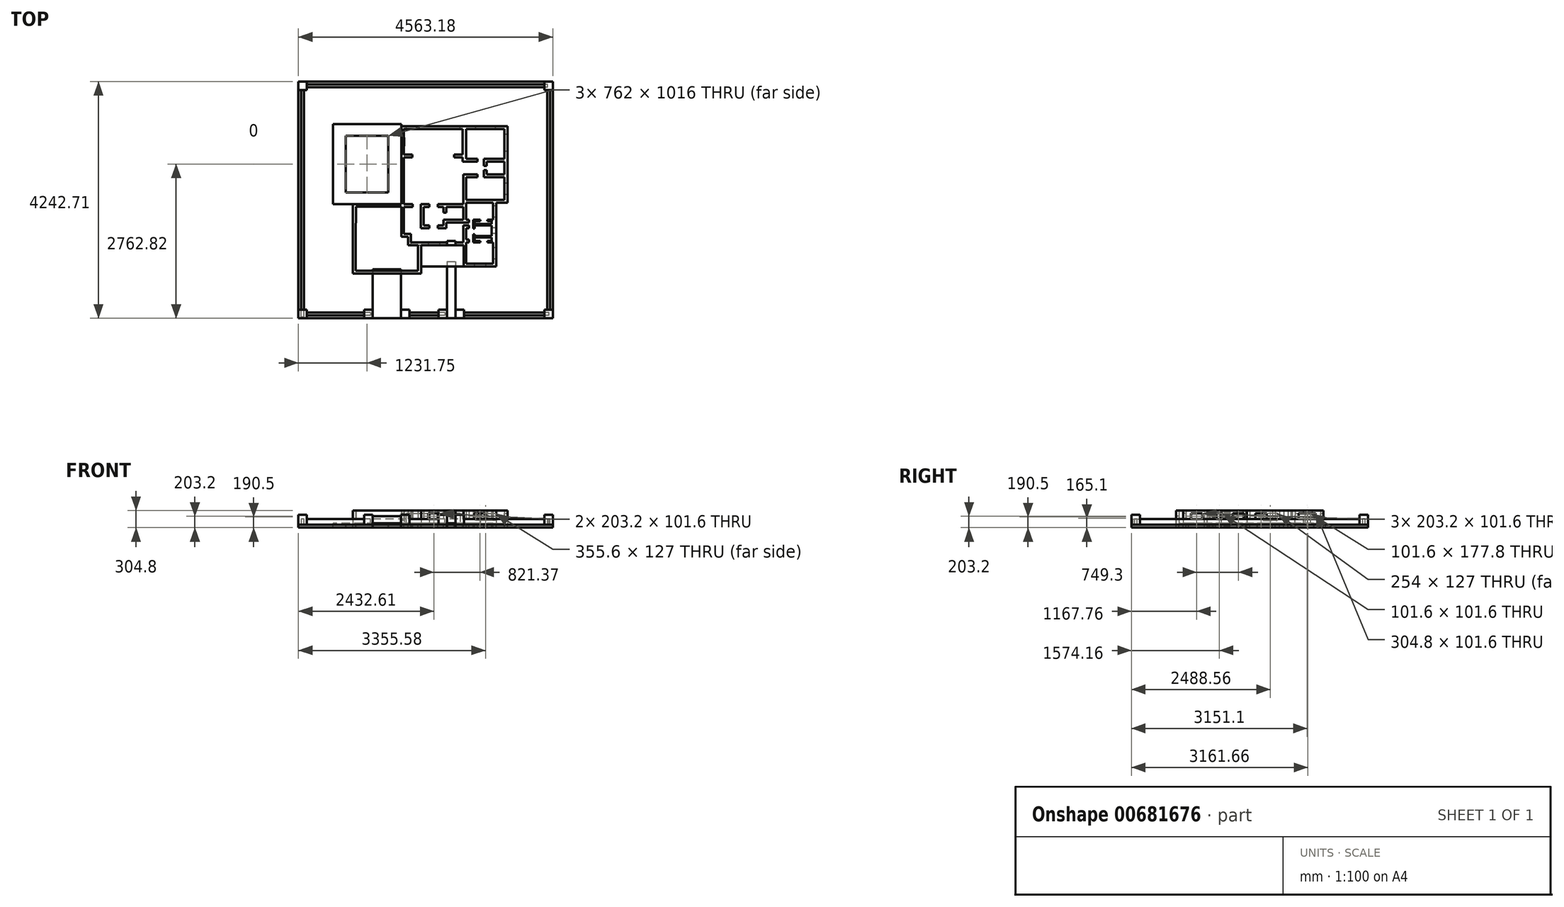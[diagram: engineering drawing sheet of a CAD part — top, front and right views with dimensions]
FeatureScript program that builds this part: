
annotation { "Feature Type Name" : "Feature", "Feature Type Description" : "" }
export const myFeature = defineFeature(function(context is Context, id is Id, definition is map)
    precondition{}
    {
        {
            var Q0;
            Q0=qCreatedBy(makeId("Top.planeOp"),FACE);
            var sketch = newSketch(context, id + "F0", { "sketchPlane" : qUnion([Q0])});
            skLineSegment(sketch, "E0", {"start": v(0, 0) * mm, "end": v(533.4, 0) * mm});
            skLineSegment(sketch, "E1", {"start": v(1396.8, 508) * mm, "end": v(1396.8, 127) * mm});
            skLineSegment(sketch, "E2", {"start": v(1396.8, 127) * mm, "end": v(1879.4, 127) * mm});
            skLineSegment(sketch, "E3", {"start": v(1828.6, 1270) * mm, "end": v(2082.6, 1270) * mm});
            skLineSegment(sketch, "E4", {"start": v(2082.6, 2540) * mm, "end": v(1396.8, 2540) * mm});
            skLineSegment(sketch, "E5", {"start": v(231.53, 1150.6) * mm, "end": v(-301.87, 1150.6) * mm});
            skLineSegment(sketch, "E6", {"start": v(-304.8, 1192.71) * mm, "end": v(177.8, 1192.71) * mm});
            skLineSegment(sketch, "E7", {"start": v(-47.87, -51.89) * mm, "end": v(587.13, -51.89) * mm});
            skLineSegment(sketch, "E8", {"start": v(587.13, -51.89) * mm, "end": v(587.13, 456.11) * mm});
            skLineSegment(sketch, "E9", {"start": v(587.13, 456.11) * mm, "end": v(1349.13, 456.11) * mm});
            skLineSegment(sketch, "E10", {"start": v(1349.13, 456.11) * mm, "end": v(1349.13, 75.11) * mm});
            skLineSegment(sketch, "E11", {"start": v(1349.13, 75.11) * mm, "end": v(1933.33, 75.11) * mm});
            skLineSegment(sketch, "E12", {"start": v(2136.53, 1218.11) * mm, "end": v(2136.53, 2589.71) * mm});
            skLineSegment(sketch, "E13", {"start": v(2136.53, 2589.71) * mm, "end": v(1349.13, 2589.71) * mm});
            skLineSegment(sketch, "E14", {"start": v(533.4, 456.11) * mm, "end": v(482.6, 456.11) * mm});
            skLineSegment(sketch, "E15", {"start": v(482.6, 456.11) * mm, "end": v(355.6, 456.11) * mm});
            skLineSegment(sketch, "E16", {"start": v(355.6, 456.11) * mm, "end": v(355.6, 608.51) * mm});
            skLineSegment(sketch, "E17", {"start": v(355.6, 608.51) * mm, "end": v(231.53, 608.51) * mm});
            skLineSegment(sketch, "E18", {"start": v(231.53, 608.51) * mm, "end": v(231.53, 1150.6) * mm});
            skLineSegment(sketch, "E19", {"start": v(279.4, 1143) * mm, "end": v(279.4, 660.4) * mm});
            skLineSegment(sketch, "E20", {"start": v(406.4, 508) * mm, "end": v(533.4, 508) * mm});
            skLineSegment(sketch, "E21", {"start": v(177.8, 1192.71) * mm, "end": v(231.53, 1192.71) * mm});
            skLineSegment(sketch, "E22", {"start": v(231.53, 1192.71) * mm, "end": v(231.53, 2081.71) * mm});
            skLineSegment(sketch, "E23", {"start": v(533.4, 456.11) * mm, "end": v(533.4, 0) * mm});
            skLineSegment(sketch, "E24", {"start": v(1828.6, 1219.2) * mm, "end": v(1396.8, 1219.2) * mm});
            skLineSegment(sketch, "E25", {"start": v(1933.33, 75.11) * mm, "end": v(1933.33, 1218.11) * mm});
            skLineSegment(sketch, "E26", {"start": v(1933.33, 1218.11) * mm, "end": v(2136.53, 1218.11) * mm});
            skLineSegment(sketch, "E27", {"start": v(1879.4, 127) * mm, "end": v(1879.4, 1219.2) * mm});
            skLineSegment(sketch, "E28", {"start": v(1879.4, 1219.2) * mm, "end": v(1828.6, 1219.2) * mm});
            skLineSegment(sketch, "E29", {"start": v(1396.8, 508) * mm, "end": v(1447.6, 508) * mm});
            skLineSegment(sketch, "E30", {"start": v(1523.8, 508) * mm, "end": v(1650.8, 508) * mm});
            skLineSegment(sketch, "E31", {"start": v(1879.4, 508) * mm, "end": v(1777.8, 508) * mm});
            skLineSegment(sketch, "E32", {"start": v(1523.8, 508) * mm, "end": v(1523.8, 596.9) * mm});
            skLineSegment(sketch, "E33", {"start": v(1879.4, 811.34) * mm, "end": v(1879.4, 749.31) * mm});
            skLineSegment(sketch, "E34", {"start": v(1523.8, 914.4) * mm, "end": v(1650.8, 914.4) * mm});
            skLineSegment(sketch, "E35", {"start": v(1879.4, 914.4) * mm, "end": v(1777.8, 914.4) * mm});
            skLineSegment(sketch, "E36", {"start": v(1523.8, 596.9) * mm, "end": v(1523.8, 650.75) * mm});
            skLineSegment(sketch, "E37", {"start": v(1523.8, 811.34) * mm, "end": v(1523.8, 757.49) * mm});
            skLineSegment(sketch, "E38", {"start": v(1396.8, 965.2) * mm, "end": v(1396.8, 1219.2) * mm});
            skLineSegment(sketch, "E39", {"start": v(1650.8, 914.4) * mm, "end": v(1650.8, 889) * mm});
            skLineSegment(sketch, "E40", {"start": v(1650.8, 889) * mm, "end": v(1549.2, 889) * mm});
            skLineSegment(sketch, "E41", {"start": v(1549.2, 889) * mm, "end": v(1549.2, 838.2) * mm});
            skLineSegment(sketch, "E42", {"start": v(1549.2, 838.2) * mm, "end": v(1854, 838.2) * mm});
            skLineSegment(sketch, "E43", {"start": v(1854, 838.2) * mm, "end": v(1854, 889) * mm});
            skLineSegment(sketch, "E44", {"start": v(1854, 889) * mm, "end": v(1777.8, 889) * mm});
            skLineSegment(sketch, "E45", {"start": v(1777.8, 889) * mm, "end": v(1777.8, 914.4) * mm});
            skLineSegment(sketch, "E46", {"start": v(1523.8, 757.49) * mm, "end": v(1549.2, 757.49) * mm});
            skLineSegment(sketch, "E47", {"start": v(1549.2, 757.49) * mm, "end": v(1549.2, 811.34) * mm});
            skLineSegment(sketch, "E48", {"start": v(1549.2, 811.34) * mm, "end": v(1854, 811.34) * mm});
            skLineSegment(sketch, "E49", {"start": v(1854, 811.34) * mm, "end": v(1854, 622.3) * mm});
            skLineSegment(sketch, "E50", {"start": v(1854, 622.3) * mm, "end": v(1549.2, 622.3) * mm});
            skLineSegment(sketch, "E51", {"start": v(1549.2, 622.3) * mm, "end": v(1549.2, 650.75) * mm});
            skLineSegment(sketch, "E52", {"start": v(1549.2, 650.75) * mm, "end": v(1523.8, 650.75) * mm});
            skLineSegment(sketch, "E53", {"start": v(1650.8, 508) * mm, "end": v(1650.8, 533.4) * mm});
            skLineSegment(sketch, "E54", {"start": v(1650.8, 533.4) * mm, "end": v(1549.2, 533.4) * mm});
            skLineSegment(sketch, "E55", {"start": v(1549.2, 533.4) * mm, "end": v(1549.2, 596.9) * mm});
            skLineSegment(sketch, "E56", {"start": v(1549.2, 596.9) * mm, "end": v(1854, 596.9) * mm});
            skLineSegment(sketch, "E57", {"start": v(1854, 596.9) * mm, "end": v(1854, 533.4) * mm});
            skLineSegment(sketch, "E58", {"start": v(1854, 533.4) * mm, "end": v(1777.8, 533.4) * mm});
            skLineSegment(sketch, "E59", {"start": v(1777.8, 533.4) * mm, "end": v(1777.8, 508) * mm});
            skLineSegment(sketch, "E60", {"start": v(1447.6, 508) * mm, "end": v(1447.6, 558.8) * mm});
            skLineSegment(sketch, "E61", {"start": v(1447.6, 558.8) * mm, "end": v(1396.8, 558.8) * mm});
            skLineSegment(sketch, "E62", {"start": v(1396.8, 558.8) * mm, "end": v(1396.8, 762) * mm});
            skLineSegment(sketch, "E63", {"start": v(1396.8, 965.2) * mm, "end": v(1396.8, 914.4) * mm});
            skLineSegment(sketch, "E64", {"start": v(1714.5, 1678.02) * mm, "end": v(2082.6, 1678.02) * mm});
            skLineSegment(sketch, "E65", {"start": v(1331.87, 2032) * mm, "end": v(1331.87, 1957.42) * mm});
            skLineSegment(sketch, "E66", {"start": v(1331.87, 1957.42) * mm, "end": v(1600.2, 1957.42) * mm});
            skLineSegment(sketch, "E67", {"start": v(1600.2, 1957.42) * mm, "end": v(1600.2, 2008.22) * mm});
            skLineSegment(sketch, "E68", {"start": v(1600.2, 2008.22) * mm, "end": v(1396.8, 2008.22) * mm});
            skLineSegment(sketch, "E69", {"start": v(1396.8, 2008.22) * mm, "end": v(1396.8, 2540) * mm});
            skLineSegment(sketch, "E70", {"start": v(1714.5, 1957.42) * mm, "end": v(1714.5, 2008.22) * mm});
            skLineSegment(sketch, "E71", {"start": v(1714.5, 2008.22) * mm, "end": v(2082.6, 2008.22) * mm});
            skLineSegment(sketch, "E72", {"start": v(2082.6, 2008.22) * mm, "end": v(2082.6, 2540) * mm});
            skLineSegment(sketch, "E73", {"start": v(1714.5, 1678.02) * mm, "end": v(1714.5, 1728.82) * mm});
            skLineSegment(sketch, "E74", {"start": v(2082.6, 1728.82) * mm, "end": v(2082.6, 1957.42) * mm});
            skLineSegment(sketch, "E75", {"start": v(2082.6, 1270) * mm, "end": v(2082.6, 1678.02) * mm});
            skLineSegment(sketch, "E76", {"start": v(1828.6, 1270) * mm, "end": v(1396.8, 1270) * mm});
            skLineSegment(sketch, "E77", {"start": v(1396.8, 1270) * mm, "end": v(1396.8, 1678.02) * mm});
            skLineSegment(sketch, "E78", {"start": v(1346, 1574.8) * mm, "end": v(1346, 1728.82) * mm});
            skLineSegment(sketch, "E79", {"start": v(1346, 1728.82) * mm, "end": v(1600.2, 1728.82) * mm});
            skLineSegment(sketch, "E80", {"start": v(1600.2, 1728.82) * mm, "end": v(1600.2, 1678.02) * mm});
            skLineSegment(sketch, "E81", {"start": v(1600.2, 1678.02) * mm, "end": v(1396.8, 1678.02) * mm});
            skLineSegment(sketch, "E82", {"start": v(1714.5, 1957.42) * mm, "end": v(1714.5, 1881.22) * mm});
            skLineSegment(sketch, "E83", {"start": v(1714.5, 1728.82) * mm, "end": v(1714.5, 1805.02) * mm});
            skLineSegment(sketch, "E84", {"start": v(1714.5, 1805.02) * mm, "end": v(1765.3, 1805.02) * mm});
            skLineSegment(sketch, "E85", {"start": v(1765.3, 1805.02) * mm, "end": v(1765.3, 1728.82) * mm});
            skLineSegment(sketch, "E86", {"start": v(1765.3, 1728.82) * mm, "end": v(2082.6, 1728.82) * mm});
            skLineSegment(sketch, "E87", {"start": v(1714.5, 1881.22) * mm, "end": v(1765.3, 1881.22) * mm});
            skLineSegment(sketch, "E88", {"start": v(1765.3, 1881.22) * mm, "end": v(1765.3, 1957.42) * mm});
            skLineSegment(sketch, "E89", {"start": v(1765.3, 1957.42) * mm, "end": v(2082.6, 1957.42) * mm});
            skLineSegment(sketch, "E90", {"start": v(-635, 508) * mm, "end": v(-635, 1192.71) * mm});
            skLineSegment(sketch, "E91", {"start": v(-635, 1192.71) * mm, "end": v(-304.8, 1192.71) * mm});
            skLineSegment(sketch, "E92", {"start": v(-301.87, 1150.6) * mm, "end": v(-581.27, 1150.6) * mm});
            skLineSegment(sketch, "E93", {"start": v(-584.2, 558.8) * mm, "end": v(-581.27, 1150.6) * mm});
            skLineSegment(sketch, "E94", {"start": v(-47.87, -51.89) * mm, "end": v(-635, -51.89) * mm});
            skLineSegment(sketch, "E95", {"start": v(-635, -51.89) * mm, "end": v(-635, 508) * mm});
            skLineSegment(sketch, "E96", {"start": v(0, 0) * mm, "end": v(-584.2, 0) * mm});
            skLineSegment(sketch, "E97", {"start": v(-584.2, 0) * mm, "end": v(-584.2, 558.8) * mm});
            skLineSegment(sketch, "E98", {"start": v(1331.87, 2032) * mm, "end": v(1179.47, 2032) * mm});
            skLineSegment(sketch, "E99", {"start": v(1179.47, 2032) * mm, "end": v(1179.47, 2081.71) * mm});
            skLineSegment(sketch, "E100", {"start": v(279.4, 2032) * mm, "end": v(431.8, 2032) * mm});
            skLineSegment(sketch, "E101", {"start": v(431.8, 2032) * mm, "end": v(431.8, 2081.71) * mm});
            skLineSegment(sketch, "E102", {"start": v(431.8, 2081.71) * mm, "end": v(279.4, 2081.71) * mm});
            skLineSegment(sketch, "E103", {"start": v(1179.47, 2081.71) * mm, "end": v(1331.87, 2081.71) * mm});
            skLineSegment(sketch, "E104", {"start": v(1331.87, 2081.71) * mm, "end": v(1331.87, 2540) * mm});
            skLineSegment(sketch, "E105", {"start": v(1331.87, 2540) * mm, "end": v(1179.47, 2540) * mm});
            skLineSegment(sketch, "E106", {"start": v(1179.47, 2589.71) * mm, "end": v(1349.13, 2589.71) * mm});
            skLineSegment(sketch, "E107", {"start": v(231.53, 2081.71) * mm, "end": v(231.53, 2589.71) * mm});
            skLineSegment(sketch, "E108", {"start": v(231.53, 2589.71) * mm, "end": v(431.8, 2589.71) * mm});
            skLineSegment(sketch, "E109", {"start": v(431.8, 2538.91) * mm, "end": v(279.4, 2538.91) * mm});
            skLineSegment(sketch, "E110", {"start": v(279.4, 2538.91) * mm, "end": v(279.4, 2081.71) * mm});
            skLineSegment(sketch, "E111", {"start": v(1346, 762) * mm, "end": v(1346, 508) * mm});
            skLineSegment(sketch, "E112", {"start": v(1346, 508) * mm, "end": v(533.4, 508) * mm});
            skLineSegment(sketch, "E113", {"start": v(1346, 863.6) * mm, "end": v(1396.8, 863.6) * mm});
            skLineSegment(sketch, "E114", {"start": v(1523.8, 811.34) * mm, "end": v(1523.8, 863.6) * mm});
            skLineSegment(sketch, "E115", {"start": v(1523.8, 863.6) * mm, "end": v(1523.8, 914.4) * mm});
            skLineSegment(sketch, "E116", {"start": v(1396.8, 914.4) * mm, "end": v(1447.6, 914.4) * mm});
            skLineSegment(sketch, "E117", {"start": v(1447.6, 914.4) * mm, "end": v(1447.6, 863.6) * mm});
            skLineSegment(sketch, "E118", {"start": v(1447.6, 863.6) * mm, "end": v(1396.8, 863.6) * mm});
            skLineSegment(sketch, "E119", {"start": v(406.4, 508) * mm, "end": v(406.4, 660.4) * mm});
            skLineSegment(sketch, "E120", {"start": v(406.4, 660.4) * mm, "end": v(279.4, 660.4) * mm});
            skLineSegment(sketch, "E121", {"start": v(1396.8, 812.8) * mm, "end": v(1447.6, 812.8) * mm});
            skLineSegment(sketch, "E122", {"start": v(1447.6, 812.8) * mm, "end": v(1447.6, 762) * mm});
            skLineSegment(sketch, "E123", {"start": v(1447.6, 762) * mm, "end": v(1396.8, 762) * mm});
            skLineSegment(sketch, "E124", {"start": v(431.8, 2538.91) * mm, "end": v(1179.47, 2540) * mm});
            skLineSegment(sketch, "E125", {"start": v(1179.47, 2589.71) * mm, "end": v(431.8, 2589.71) * mm});
            skLineSegment(sketch, "E126", {"start": v(1346, 812.8) * mm, "end": v(1396.8, 812.8) * mm});
            skLineSegment(sketch, "E127", {"start": v(1346, 508) * mm, "end": v(1041.2, 508) * mm});
            skLineSegment(sketch, "E128", {"start": v(887.59, 812.8) * mm, "end": v(887.59, 762) * mm});
            skLineSegment(sketch, "E129", {"start": v(887.59, 812.8) * mm, "end": v(938.39, 812.8) * mm});
            skLineSegment(sketch, "E130", {"start": v(1346, 1574.8) * mm, "end": v(1346, 1320.8) * mm});
            skLineSegment(sketch, "E131", {"start": v(887.59, 762) * mm, "end": v(1039.99, 762) * mm});
            skLineSegment(sketch, "E132", {"start": v(1039.99, 762) * mm, "end": v(1039.99, 812.8) * mm});
            skLineSegment(sketch, "E133", {"start": v(1346, 1320.8) * mm, "end": v(1346, 1270) * mm});
            skLineSegment(sketch, "E134", {"start": v(735.19, 762) * mm, "end": v(582.79, 762) * mm});
            skLineSegment(sketch, "E135", {"start": v(582.79, 762) * mm, "end": v(582.79, 812.8) * mm});
            skLineSegment(sketch, "E136", {"start": v(735.19, 812.8) * mm, "end": v(735.19, 762) * mm});
            skLineSegment(sketch, "E137", {"start": v(279.4, 1143) * mm, "end": v(437.73, 1143) * mm});
            skLineSegment(sketch, "E138", {"start": v(735.19, 1143) * mm, "end": v(735.19, 1193.8) * mm});
            skLineSegment(sketch, "E139", {"start": v(735.19, 1193.8) * mm, "end": v(582.79, 1193.8) * mm});
            skLineSegment(sketch, "E140", {"start": v(582.79, 1193.8) * mm, "end": v(582.79, 1143) * mm});
            skLineSegment(sketch, "E141", {"start": v(437.73, 1143) * mm, "end": v(437.73, 1193.8) * mm});
            skLineSegment(sketch, "E142", {"start": v(437.73, 1193.8) * mm, "end": v(279.4, 1193.8) * mm});
            skLineSegment(sketch, "E143", {"start": v(938.39, 812.8) * mm, "end": v(989.19, 812.8) * mm});
            skLineSegment(sketch, "E144", {"start": v(582.79, 812.8) * mm, "end": v(582.79, 1143) * mm});
            skLineSegment(sketch, "E145", {"start": v(633.59, 1143) * mm, "end": v(633.59, 812.8) * mm});
            skLineSegment(sketch, "E146", {"start": v(1039.99, 1193.8) * mm, "end": v(887.59, 1193.8) * mm});
            skLineSegment(sketch, "E147", {"start": v(887.59, 1193.8) * mm, "end": v(887.59, 1143) * mm});
            skLineSegment(sketch, "E148", {"start": v(887.59, 1143) * mm, "end": v(989.19, 1143) * mm});
            skLineSegment(sketch, "E149", {"start": v(633.59, 1143) * mm, "end": v(735.19, 1143) * mm});
            skLineSegment(sketch, "E150", {"start": v(633.59, 812.8) * mm, "end": v(735.19, 812.8) * mm});
            skLineSegment(sketch, "E151", {"start": v(279.4, 2032) * mm, "end": v(279.4, 1193.8) * mm});
            skLineSegment(sketch, "E152", {"start": v(1346, 1193.8) * mm, "end": v(1193.6, 1193.8) * mm});
            skPoint(sketch, "E152.startSnap0", {"position": v(963.79, 1193.8) * mm});
            skPoint(sketch, "E152.endSnap0", {"position": v(358.57, 1193.8) * mm});
            skLineSegment(sketch, "E153", {"start": v(1193.6, 1143) * mm, "end": v(1346, 1143) * mm});
            skLineSegment(sketch, "E154", {"start": v(1346, 1193.8) * mm, "end": v(1346, 1270) * mm});
            skLineSegment(sketch, "E155", {"start": v(1346, 762) * mm, "end": v(1346, 812.8) * mm});
            skLineSegment(sketch, "E156", {"start": v(1039.99, 1193.8) * mm, "end": v(1193.6, 1193.8) * mm});
            skLineSegment(sketch, "E157", {"start": v(1193.6, 1143) * mm, "end": v(1039.99, 1143) * mm});
            skLineSegment(sketch, "E158", {"start": v(1039.99, 863.6) * mm, "end": v(1039.99, 812.8) * mm});
            skLineSegment(sketch, "E159", {"start": v(1346, 939.8) * mm, "end": v(1346, 1117.6) * mm});
            skLineSegment(sketch, "E160", {"start": v(1346, 1117.6) * mm, "end": v(1346, 1143) * mm});
            skLineSegment(sketch, "E161", {"start": v(1346, 914.4) * mm, "end": v(1346, 939.8) * mm});
            skLineSegment(sketch, "E162", {"start": v(1346, 863.6) * mm, "end": v(1039.99, 863.6) * mm});
            skLineSegment(sketch, "E163", {"start": v(1346, 914.4) * mm, "end": v(1039.99, 914.4) * mm});
            skLineSegment(sketch, "E164", {"start": v(989.19, 914.4) * mm, "end": v(1039.99, 914.4) * mm});
            skLineSegment(sketch, "E165", {"start": v(989.19, 812.8) * mm, "end": v(989.19, 914.4) * mm});
            skLineSegment(sketch, "E166", {"start": v(989.19, 1143) * mm, "end": v(989.19, 1041.4) * mm});
            skLineSegment(sketch, "E167", {"start": v(989.19, 1041.4) * mm, "end": v(1039.99, 1041.4) * mm});
            skLineSegment(sketch, "E168", {"start": v(1039.99, 1041.4) * mm, "end": v(1039.99, 1143) * mm});
            skSolve(sketch);
        }
        {
            var Q0;
            Q0=makeQuery(id+"F0.imprint","IMPRINT",FACE,{"disambiguationData":[TD([[makeQuery(id+"F0.imprint","IMPRINT",EDGE,{"derivedFrom":sQuery(id+"F0.wireOp",EDGE,"E0")}),-1.0]])]});
            var Q1;
            Q1=makeQuery(id+"F0.imprint","IMPRINT",FACE,{"disambiguationData":[TD([[makeQuery(id+"F0.imprint","IMPRINT",EDGE,{"derivedFrom":sQuery(id+"F0.wireOp",EDGE,"E30")}),1.0]])]});
            extrude(context, id + "F1", {"entities" : qUnion([Q0, Q1]), "depth" : 254 * mm, "offsetDistance" : 25.4 * mm});
        }
        {
            var Q0;
            Q0 = qSketchRegion(id + "F0", true);
            var Q1;
            Q1=makeQuery(id+"F0.imprint","IMPRINT",FACE,{"disambiguationData":[TD([[makeQuery(id+"F0.imprint","IMPRINT",EDGE,{"derivedFrom":sQuery(id+"F0.wireOp",EDGE,"E134")}),-1.0]])]});
            var Q2;
            Q2=makeQuery(id+"F0.imprint","IMPRINT",FACE,{"disambiguationData":[TD([[makeQuery(id+"F0.imprint","IMPRINT",EDGE,{"derivedFrom":sQuery(id+"F0.wireOp",EDGE,"E128")}),1.0]])]});
            extrude(context, id + "F2", {"entities" : qUnion([Q0, Q1, Q2]), "operationType" : NewBodyOperationType.ADD, "depth" : 254 * mm, "offsetDistance" : 25.4 * mm});
        }
        {
            var Q0;
            Q0=makeQuery(id+"F1.opExtrude","CAP_FACE",FACE,{"disambiguationData":[OSD([sQuery(id+"F0.wireOp",EDGE,"E0"),sQuery(id+"F0.wireOp",EDGE,"E1"),sQuery(id+"F0.wireOp",EDGE,"E2"),sQuery(id+"F0.wireOp",EDGE,"E3"),sQuery(id+"F0.wireOp",EDGE,"E4"),sQuery(id+"F0.wireOp",EDGE,"E5"),sQuery(id+"F0.wireOp",EDGE,"E6"),sQuery(id+"F0.wireOp",EDGE,"E7"),sQuery(id+"F0.wireOp",EDGE,"E8"),sQuery(id+"F0.wireOp",EDGE,"E9"),sQuery(id+"F0.wireOp",EDGE,"E10"),sQuery(id+"F0.wireOp",EDGE,"E11"),sQuery(id+"F0.wireOp",EDGE,"E12"),sQuery(id+"F0.wireOp",EDGE,"E13"),sQuery(id+"F0.wireOp",EDGE,"E14"),sQuery(id+"F0.wireOp",EDGE,"E15"),sQuery(id+"F0.wireOp",EDGE,"E16"),sQuery(id+"F0.wireOp",EDGE,"E17"),sQuery(id+"F0.wireOp",EDGE,"E18"),sQuery(id+"F0.wireOp",EDGE,"E19"),sQuery(id+"F0.wireOp",EDGE,"E20"),sQuery(id+"F0.wireOp",EDGE,"E21"),sQuery(id+"F0.wireOp",EDGE,"E22"),sQuery(id+"F0.wireOp",EDGE,"E23"),sQuery(id+"F0.wireOp",EDGE,"E24"),sQuery(id+"F0.wireOp",EDGE,"E25"),sQuery(id+"F0.wireOp",EDGE,"E26"),sQuery(id+"F0.wireOp",EDGE,"E27"),sQuery(id+"F0.wireOp",EDGE,"E28"),sQuery(id+"F0.wireOp",EDGE,"E29"),sQuery(id+"F0.wireOp",EDGE,"E30"),sQuery(id+"F0.wireOp",EDGE,"E31"),sQuery(id+"F0.wireOp",EDGE,"E32"),sQuery(id+"F0.wireOp",EDGE,"E34"),sQuery(id+"F0.wireOp",EDGE,"E35"),sQuery(id+"F0.wireOp",EDGE,"E36"),sQuery(id+"F0.wireOp",EDGE,"E37"),sQuery(id+"F0.wireOp",EDGE,"E38"),sQuery(id+"F0.wireOp",EDGE,"E39"),sQuery(id+"F0.wireOp",EDGE,"E40"),sQuery(id+"F0.wireOp",EDGE,"E41"),sQuery(id+"F0.wireOp",EDGE,"E42"),sQuery(id+"F0.wireOp",EDGE,"E43"),sQuery(id+"F0.wireOp",EDGE,"E44"),sQuery(id+"F0.wireOp",EDGE,"E45"),sQuery(id+"F0.wireOp",EDGE,"E46"),sQuery(id+"F0.wireOp",EDGE,"E47"),sQuery(id+"F0.wireOp",EDGE,"E48"),sQuery(id+"F0.wireOp",EDGE,"E49"),sQuery(id+"F0.wireOp",EDGE,"E50"),sQuery(id+"F0.wireOp",EDGE,"E51"),sQuery(id+"F0.wireOp",EDGE,"E52"),sQuery(id+"F0.wireOp",EDGE,"E53"),sQuery(id+"F0.wireOp",EDGE,"E54"),sQuery(id+"F0.wireOp",EDGE,"E55"),sQuery(id+"F0.wireOp",EDGE,"E56"),sQuery(id+"F0.wireOp",EDGE,"E57"),sQuery(id+"F0.wireOp",EDGE,"E58"),sQuery(id+"F0.wireOp",EDGE,"E59"),sQuery(id+"F0.wireOp",EDGE,"E60"),sQuery(id+"F0.wireOp",EDGE,"E61"),sQuery(id+"F0.wireOp",EDGE,"E62"),sQuery(id+"F0.wireOp",EDGE,"E63"),sQuery(id+"F0.wireOp",EDGE,"E64"),sQuery(id+"F0.wireOp",EDGE,"E65"),sQuery(id+"F0.wireOp",EDGE,"E66"),sQuery(id+"F0.wireOp",EDGE,"E67"),sQuery(id+"F0.wireOp",EDGE,"E68"),sQuery(id+"F0.wireOp",EDGE,"E69"),sQuery(id+"F0.wireOp",EDGE,"E70"),sQuery(id+"F0.wireOp",EDGE,"E71"),sQuery(id+"F0.wireOp",EDGE,"E72"),sQuery(id+"F0.wireOp",EDGE,"E73"),sQuery(id+"F0.wireOp",EDGE,"E74"),sQuery(id+"F0.wireOp",EDGE,"E75"),sQuery(id+"F0.wireOp",EDGE,"E76"),sQuery(id+"F0.wireOp",EDGE,"E77"),sQuery(id+"F0.wireOp",EDGE,"E78"),sQuery(id+"F0.wireOp",EDGE,"E79"),sQuery(id+"F0.wireOp",EDGE,"E80"),sQuery(id+"F0.wireOp",EDGE,"E81"),sQuery(id+"F0.wireOp",EDGE,"E82"),sQuery(id+"F0.wireOp",EDGE,"E83"),sQuery(id+"F0.wireOp",EDGE,"E84"),sQuery(id+"F0.wireOp",EDGE,"E85"),sQuery(id+"F0.wireOp",EDGE,"E86"),sQuery(id+"F0.wireOp",EDGE,"E87"),sQuery(id+"F0.wireOp",EDGE,"E88"),sQuery(id+"F0.wireOp",EDGE,"E89"),sQuery(id+"F0.wireOp",EDGE,"E90"),sQuery(id+"F0.wireOp",EDGE,"E91"),sQuery(id+"F0.wireOp",EDGE,"E92"),sQuery(id+"F0.wireOp",EDGE,"E93"),sQuery(id+"F0.wireOp",EDGE,"E94"),sQuery(id+"F0.wireOp",EDGE,"E95"),sQuery(id+"F0.wireOp",EDGE,"E96"),sQuery(id+"F0.wireOp",EDGE,"E97"),sQuery(id+"F0.wireOp",EDGE,"E98"),sQuery(id+"F0.wireOp",EDGE,"E99"),sQuery(id+"F0.wireOp",EDGE,"E100"),sQuery(id+"F0.wireOp",EDGE,"E101"),sQuery(id+"F0.wireOp",EDGE,"E102"),sQuery(id+"F0.wireOp",EDGE,"E103"),sQuery(id+"F0.wireOp",EDGE,"E104"),sQuery(id+"F0.wireOp",EDGE,"E105"),sQuery(id+"F0.wireOp",EDGE,"E106"),sQuery(id+"F0.wireOp",EDGE,"E107"),sQuery(id+"F0.wireOp",EDGE,"E108"),sQuery(id+"F0.wireOp",EDGE,"E109"),sQuery(id+"F0.wireOp",EDGE,"E110"),sQuery(id+"F0.wireOp",EDGE,"E111"),sQuery(id+"F0.wireOp",EDGE,"E112"),sQuery(id+"F0.wireOp",EDGE,"E113"),sQuery(id+"F0.wireOp",EDGE,"E114"),sQuery(id+"F0.wireOp",EDGE,"E115"),sQuery(id+"F0.wireOp",EDGE,"E116"),sQuery(id+"F0.wireOp",EDGE,"E117"),sQuery(id+"F0.wireOp",EDGE,"E118"),sQuery(id+"F0.wireOp",EDGE,"E119"),sQuery(id+"F0.wireOp",EDGE,"E120"),sQuery(id+"F0.wireOp",EDGE,"E121"),sQuery(id+"F0.wireOp",EDGE,"E122"),sQuery(id+"F0.wireOp",EDGE,"E123"),sQuery(id+"F0.wireOp",EDGE,"E124"),sQuery(id+"F0.wireOp",EDGE,"E125"),sQuery(id+"F0.wireOp",EDGE,"E126"),sQuery(id+"F0.wireOp",EDGE,"E127"),sQuery(id+"F0.wireOp",EDGE,"E130"),sQuery(id+"F0.wireOp",EDGE,"wEKJqsZE-Lnf2-Pc3B-vstB-3JEagEBnImep"),sQuery(id+"F0.wireOp",EDGE,"E133"),sQuery(id+"F0.wireOp",EDGE,"E137"),sQuery(id+"F0.wireOp",EDGE,"E141"),sQuery(id+"F0.wireOp",EDGE,"E142"),sQuery(id+"F0.wireOp",EDGE,"E151"),sQuery(id+"F0.wireOp",EDGE,"E152"),sQuery(id+"F0.wireOp",EDGE,"XqZMZlJO-xrwS-6yc9-YKlE-u4GM9skw6DG2"),sQuery(id+"F0.wireOp",EDGE,"E153"),sQuery(id+"F0.wireOp",EDGE,"E154"),sQuery(id+"F0.wireOp",EDGE,"MRLSVep9-wh13-aC8x-J69K-2GoYUCsBfXyJ"),sQuery(id+"F0.wireOp",EDGE,"E155")])],"isStart":true});
            var sketch = newSketch(context, id + "F3", { "sketchPlane" : qUnion([Q0])});
            skSolve(sketch);
        }
        {
            var Q0;
            Q0=makeQuery(id+"F3.imprint","IMPRINT",FACE,{"disambiguationData":[TD([[makeQuery(id+"F3.imprint","IMPRINT",EDGE,{"derivedFrom":makeQuery(id+"F1.opExtrude","CAP_EDGE",EDGE,{"disambiguationData":[OSD([sQuery(id+"F0.wireOp",EDGE,"E16")])],"isStart":true})}),-1.0]])]});
            var Q1;
            Q1=makeQuery(id+"F3.imprint","IMPRINT",FACE,{"disambiguationData":[TD([[makeQuery(id+"F3.imprint","IMPRINT",EDGE,{"derivedFrom":makeQuery(id+"F1.opExtrude","CAP_EDGE",EDGE,{"disambiguationData":[OSD([sQuery(id+"F0.wireOp",EDGE,"E1")])],"isStart":true})}),-1.0]])]});
            extrude(context, id + "F4", {"entities" : qUnion([Q0, Q1]), "oppositeDirection" : true, "depth" : 25.4 * mm, "offsetDistance" : 25.4 * mm});
        }
        {
            var Q0;
            Q0=makeQuery(id+"F1.opExtrude","SWEPT_FACE",FACE,{"disambiguationData":[OSD([sQuery(id+"F0.wireOp",EDGE,"E18")])]});
            var sketch = newSketch(context, id + "F5", { "sketchPlane" : qUnion([Q0])});
            skLineSegment(sketch, "E169", {"start": v(-608.51, 254) * mm, "end": v(-879.56, 254) * mm});
            skLineSegment(sketch, "E170", {"start": v(-879.56, 254) * mm, "end": v(-981.16, 254) * mm});
            skLineSegment(sketch, "E171", {"start": v(-981.16, 254) * mm, "end": v(-777.96, 254) * mm});
            skLineSegment(sketch, "E172", {"start": v(-777.96, 254) * mm, "end": v(-777.96, 25.4) * mm});
            skLineSegment(sketch, "E173", {"start": v(-777.96, 25.4) * mm, "end": v(-981.16, 25.4) * mm});
            skLineSegment(sketch, "E174", {"start": v(-981.16, 25.4) * mm, "end": v(-981.16, 254) * mm});
            skLineSegment(sketch, "E175", {"start": v(-981.16, 254) * mm, "end": v(-981.16, 203.2) * mm});
            skLineSegment(sketch, "E176", {"start": v(-981.16, 203.2) * mm, "end": v(-777.96, 203.2) * mm});
            skLineSegment(sketch, "E177", {"start": v(-777.96, 203.2) * mm, "end": v(-777.96, 254) * mm});
            skSolve(sketch);
        }
        {
            var Q0;
            Q0 = qSketchRegion(id + "F5", true);
            extrude(context, id + "F6", {"entities" : qUnion([Q0]), "operationType" : NewBodyOperationType.REMOVE, "oppositeDirection" : true, "depth" : 50.8 * mm, "offsetDistance" : 25.4 * mm});
        }
        {
            var Q0;
            Q0=makeQuery(id+"F1.opExtrude","SWEPT_FACE",FACE,{"disambiguationData":[OSD([sQuery(id+"F0.wireOp",EDGE,"E9")])]});
            var sketch = newSketch(context, id + "F7", { "sketchPlane" : qUnion([Q0])});
            skLineSegment(sketch, "E178", {"start": v(1052.6, 0) * mm, "end": v(1052.6, 254) * mm});
            skLineSegment(sketch, "E179", {"start": v(1052.6, 254) * mm, "end": v(1205, 254) * mm});
            skLineSegment(sketch, "E180", {"start": v(1205, 254) * mm, "end": v(1205, 0) * mm});
            skLineSegment(sketch, "E181", {"start": v(1205, 0) * mm, "end": v(1052.6, 0) * mm});
            skSolve(sketch);
        }
        {
            var Q0;
            Q0 = qSketchRegion(id + "F7", true);
            extrude(context, id + "F8", {"entities" : qUnion([Q0]), "operationType" : NewBodyOperationType.REMOVE, "oppositeDirection" : true, "depth" : 76.2 * mm, "offsetDistance" : 25.4 * mm});
        }
        {
            var Q0;
            Q0=makeQuery(id+"F4.opExtrude","SWEPT_FACE",FACE,{"disambiguationData":[OSD([sQuery(id+"F0.wireOp",EDGE,"E20"),sQuery(id+"F0.wireOp",EDGE,"E112"),sQuery(id+"F0.wireOp",EDGE,"E127")])]});
            var sketch = newSketch(context, id + "F9", { "sketchPlane" : qUnion([Q0])});
            skSolve(sketch);
        }
        {
            var Q0;
            Q0 = qSketchRegion(id + "F9", true);
            var Q1;
            {var subQ0=sQuery(id+"F0.wireOp",EDGE,"E127");var subQ1=sQuery(id+"F0.wireOp",EDGE,"E112");var subQ2=sQuery(id+"F0.wireOp",EDGE,"E20");Q1=makeQuery(id+"F9.imprint","IMPRINT",FACE,{"disambiguationData":[TD([[makeQuery(id+"F9.imprint","IMPRINT",EDGE,{"derivedFrom":makeQuery(id+"F4.opExtrude","CAP_EDGE",EDGE,{"disambiguationData":[OSD([subQ2,subQ1,subQ0])],"isStart":true})}),-1.0]])]});}
            extrude(context, id + "F10", {"entities" : qUnion([Q0, Q1]), "depth" : 53.34 * mm, "offsetDistance" : 25.4 * mm});
        }
        {
            var Q0;
            {var subQ130=sQuery(id+"F0.wireOp",EDGE,"E9");var subQ131=sQuery(id+"F0.wireOp",EDGE,"E8");Q0=makeQuery(id+"F8.boolean.opBoolean","SPLIT",FACE,{"disambiguationData":[TD([makeQuery(id+"F1.opExtrude","SWEPT_FACE",FACE,{"disambiguationData":[OSD([subQ131])]})])],"derivedFrom":makeQuery(id+"F1.opExtrude","SWEPT_FACE",FACE,{"disambiguationData":[OSD([subQ130])]})});}
            var sketch = newSketch(context, id + "F11", { "sketchPlane" : qUnion([Q0])});
            skLineSegment(sketch, "E182", {"start": v(819.86, 203.2) * mm, "end": v(718.26, 203.2) * mm});
            skLineSegment(sketch, "E183", {"start": v(718.26, 203.2) * mm, "end": v(718.26, 101.6) * mm});
            skLineSegment(sketch, "E184", {"start": v(718.26, 101.6) * mm, "end": v(921.46, 101.6) * mm});
            skLineSegment(sketch, "E185", {"start": v(921.46, 101.6) * mm, "end": v(921.46, 203.2) * mm});
            skLineSegment(sketch, "E186", {"start": v(921.46, 203.2) * mm, "end": v(819.86, 203.2) * mm});
            skSolve(sketch);
        }
        {
            var Q0;
            Q0 = qSketchRegion(id + "F11", true);
            extrude(context, id + "F12", {"entities" : qUnion([Q0]), "operationType" : NewBodyOperationType.REMOVE, "oppositeDirection" : true, "depth" : 63.5 * mm, "offsetDistance" : 25.4 * mm});
        }
        {
            var Q0;
            Q0=makeQuery(id+"F1.opExtrude","SWEPT_FACE",FACE,{"disambiguationData":[OSD([sQuery(id+"F0.wireOp",EDGE,"E11")])]});
            var sketch = newSketch(context, id + "F13", { "sketchPlane" : qUnion([Q0])});
            skLineSegment(sketch, "E187", {"start": v(1641.23, 203.2) * mm, "end": v(1539.63, 203.2) * mm});
            skLineSegment(sketch, "E188", {"start": v(1539.63, 203.2) * mm, "end": v(1539.63, 101.6) * mm});
            skLineSegment(sketch, "E189", {"start": v(1539.63, 101.6) * mm, "end": v(1742.83, 101.6) * mm});
            skLineSegment(sketch, "E190", {"start": v(1742.83, 101.6) * mm, "end": v(1742.83, 203.2) * mm});
            skLineSegment(sketch, "E191", {"start": v(1742.83, 203.2) * mm, "end": v(1641.23, 203.2) * mm});
            skSolve(sketch);
        }
        {
            var Q0;
            Q0 = qSketchRegion(id + "F13", true);
            extrude(context, id + "F14", {"entities" : qUnion([Q0]), "operationType" : NewBodyOperationType.REMOVE, "oppositeDirection" : true, "depth" : 76.2 * mm, "offsetDistance" : 25.4 * mm});
        }
        {
            var Q0;
            Q0=makeQuery(id+"F1.opExtrude","SWEPT_FACE",FACE,{"disambiguationData":[OSD([sQuery(id+"F0.wireOp",EDGE,"E25")])]});
            var sketch = newSketch(context, id + "F15", { "sketchPlane" : qUnion([Q0])});
            skLineSegment(sketch, "E192", {"start": v(75.11, 254) * mm, "end": v(557.71, 254) * mm});
            skLineSegment(sketch, "E193", {"start": v(557.71, 254) * mm, "end": v(316.41, 254) * mm});
            skLineSegment(sketch, "E194", {"start": v(316.41, 203.2) * mm, "end": v(214.81, 203.2) * mm});
            skLineSegment(sketch, "E195", {"start": v(214.81, 203.2) * mm, "end": v(214.81, 101.6) * mm});
            skLineSegment(sketch, "E196", {"start": v(214.81, 101.6) * mm, "end": v(418.01, 101.6) * mm});
            skLineSegment(sketch, "E197", {"start": v(418.01, 101.6) * mm, "end": v(418.01, 203.2) * mm});
            skLineSegment(sketch, "E198", {"start": v(418.01, 203.2) * mm, "end": v(316.41, 203.2) * mm});
            skLineSegment(sketch, "E199", {"start": v(1218.11, 254) * mm, "end": v(913.31, 254) * mm});
            skLineSegment(sketch, "E200", {"start": v(1065.71, 203.2) * mm, "end": v(964.11, 203.2) * mm});
            skLineSegment(sketch, "E201", {"start": v(964.11, 203.2) * mm, "end": v(964.11, 101.6) * mm});
            skLineSegment(sketch, "E202", {"start": v(964.11, 101.6) * mm, "end": v(1167.31, 101.6) * mm});
            skLineSegment(sketch, "E203", {"start": v(1167.31, 101.6) * mm, "end": v(1167.31, 203.2) * mm});
            skLineSegment(sketch, "E204", {"start": v(1167.31, 203.2) * mm, "end": v(1065.71, 203.2) * mm});
            skLineSegment(sketch, "E205", {"start": v(913.31, 254) * mm, "end": v(862.51, 254) * mm});
            skLineSegment(sketch, "E206", {"start": v(862.51, 254) * mm, "end": v(557.71, 254) * mm});
            skLineSegment(sketch, "E207", {"start": v(710.11, 254) * mm, "end": v(710.11, 203.2) * mm});
            skLineSegment(sketch, "E208", {"start": v(710.11, 203.2) * mm, "end": v(672.01, 203.2) * mm});
            skLineSegment(sketch, "E209", {"start": v(672.01, 203.2) * mm, "end": v(672.01, 101.6) * mm});
            skLineSegment(sketch, "E210", {"start": v(672.01, 101.6) * mm, "end": v(773.61, 101.6) * mm});
            skLineSegment(sketch, "E211", {"start": v(773.61, 101.6) * mm, "end": v(773.61, 203.2) * mm});
            skLineSegment(sketch, "E212", {"start": v(773.61, 203.2) * mm, "end": v(710.11, 203.2) * mm});
            skSolve(sketch);
        }
        {
            var Q0;
            Q0 = qSketchRegion(id + "F15", true);
            extrude(context, id + "F16", {"entities" : qUnion([Q0]), "operationType" : NewBodyOperationType.REMOVE, "oppositeDirection" : true, "depth" : 101.6 * mm, "offsetDistance" : 25.4 * mm});
        }
        {
            var Q0;
            Q0=makeQuery(id+"F1.opExtrude","CAP_FACE",FACE,{"disambiguationData":[OSD([sQuery(id+"F0.wireOp",EDGE,"E0"),sQuery(id+"F0.wireOp",EDGE,"E1"),sQuery(id+"F0.wireOp",EDGE,"E2"),sQuery(id+"F0.wireOp",EDGE,"E3"),sQuery(id+"F0.wireOp",EDGE,"E4"),sQuery(id+"F0.wireOp",EDGE,"E5"),sQuery(id+"F0.wireOp",EDGE,"E6"),sQuery(id+"F0.wireOp",EDGE,"E7"),sQuery(id+"F0.wireOp",EDGE,"E8"),sQuery(id+"F0.wireOp",EDGE,"E9"),sQuery(id+"F0.wireOp",EDGE,"E10"),sQuery(id+"F0.wireOp",EDGE,"E11"),sQuery(id+"F0.wireOp",EDGE,"E12"),sQuery(id+"F0.wireOp",EDGE,"E13"),sQuery(id+"F0.wireOp",EDGE,"E14"),sQuery(id+"F0.wireOp",EDGE,"E15"),sQuery(id+"F0.wireOp",EDGE,"E16"),sQuery(id+"F0.wireOp",EDGE,"E17"),sQuery(id+"F0.wireOp",EDGE,"E18"),sQuery(id+"F0.wireOp",EDGE,"E19"),sQuery(id+"F0.wireOp",EDGE,"E20"),sQuery(id+"F0.wireOp",EDGE,"E21"),sQuery(id+"F0.wireOp",EDGE,"E22"),sQuery(id+"F0.wireOp",EDGE,"E23"),sQuery(id+"F0.wireOp",EDGE,"E24"),sQuery(id+"F0.wireOp",EDGE,"E25"),sQuery(id+"F0.wireOp",EDGE,"E26"),sQuery(id+"F0.wireOp",EDGE,"E27"),sQuery(id+"F0.wireOp",EDGE,"E28"),sQuery(id+"F0.wireOp",EDGE,"E29"),sQuery(id+"F0.wireOp",EDGE,"E30"),sQuery(id+"F0.wireOp",EDGE,"E31"),sQuery(id+"F0.wireOp",EDGE,"E32"),sQuery(id+"F0.wireOp",EDGE,"E34"),sQuery(id+"F0.wireOp",EDGE,"E35"),sQuery(id+"F0.wireOp",EDGE,"E36"),sQuery(id+"F0.wireOp",EDGE,"E37"),sQuery(id+"F0.wireOp",EDGE,"E38"),sQuery(id+"F0.wireOp",EDGE,"E39"),sQuery(id+"F0.wireOp",EDGE,"E40"),sQuery(id+"F0.wireOp",EDGE,"E41"),sQuery(id+"F0.wireOp",EDGE,"E42"),sQuery(id+"F0.wireOp",EDGE,"E43"),sQuery(id+"F0.wireOp",EDGE,"E44"),sQuery(id+"F0.wireOp",EDGE,"E45"),sQuery(id+"F0.wireOp",EDGE,"E46"),sQuery(id+"F0.wireOp",EDGE,"E47"),sQuery(id+"F0.wireOp",EDGE,"E48"),sQuery(id+"F0.wireOp",EDGE,"E49"),sQuery(id+"F0.wireOp",EDGE,"E50"),sQuery(id+"F0.wireOp",EDGE,"E51"),sQuery(id+"F0.wireOp",EDGE,"E52"),sQuery(id+"F0.wireOp",EDGE,"E53"),sQuery(id+"F0.wireOp",EDGE,"E54"),sQuery(id+"F0.wireOp",EDGE,"E55"),sQuery(id+"F0.wireOp",EDGE,"E56"),sQuery(id+"F0.wireOp",EDGE,"E57"),sQuery(id+"F0.wireOp",EDGE,"E58"),sQuery(id+"F0.wireOp",EDGE,"E59"),sQuery(id+"F0.wireOp",EDGE,"E60"),sQuery(id+"F0.wireOp",EDGE,"E61"),sQuery(id+"F0.wireOp",EDGE,"E62"),sQuery(id+"F0.wireOp",EDGE,"E63"),sQuery(id+"F0.wireOp",EDGE,"E64"),sQuery(id+"F0.wireOp",EDGE,"E65"),sQuery(id+"F0.wireOp",EDGE,"E66"),sQuery(id+"F0.wireOp",EDGE,"E67"),sQuery(id+"F0.wireOp",EDGE,"E68"),sQuery(id+"F0.wireOp",EDGE,"E69"),sQuery(id+"F0.wireOp",EDGE,"E70"),sQuery(id+"F0.wireOp",EDGE,"E71"),sQuery(id+"F0.wireOp",EDGE,"E72"),sQuery(id+"F0.wireOp",EDGE,"E73"),sQuery(id+"F0.wireOp",EDGE,"E74"),sQuery(id+"F0.wireOp",EDGE,"E75"),sQuery(id+"F0.wireOp",EDGE,"E76"),sQuery(id+"F0.wireOp",EDGE,"E77"),sQuery(id+"F0.wireOp",EDGE,"E78"),sQuery(id+"F0.wireOp",EDGE,"E79"),sQuery(id+"F0.wireOp",EDGE,"E80"),sQuery(id+"F0.wireOp",EDGE,"E81"),sQuery(id+"F0.wireOp",EDGE,"E82"),sQuery(id+"F0.wireOp",EDGE,"E83"),sQuery(id+"F0.wireOp",EDGE,"E84"),sQuery(id+"F0.wireOp",EDGE,"E85"),sQuery(id+"F0.wireOp",EDGE,"E86"),sQuery(id+"F0.wireOp",EDGE,"E87"),sQuery(id+"F0.wireOp",EDGE,"E88"),sQuery(id+"F0.wireOp",EDGE,"E89"),sQuery(id+"F0.wireOp",EDGE,"E90"),sQuery(id+"F0.wireOp",EDGE,"E91"),sQuery(id+"F0.wireOp",EDGE,"E92"),sQuery(id+"F0.wireOp",EDGE,"E93"),sQuery(id+"F0.wireOp",EDGE,"E94"),sQuery(id+"F0.wireOp",EDGE,"E95"),sQuery(id+"F0.wireOp",EDGE,"E96"),sQuery(id+"F0.wireOp",EDGE,"E97"),sQuery(id+"F0.wireOp",EDGE,"E98"),sQuery(id+"F0.wireOp",EDGE,"E99"),sQuery(id+"F0.wireOp",EDGE,"E100"),sQuery(id+"F0.wireOp",EDGE,"E101"),sQuery(id+"F0.wireOp",EDGE,"E102"),sQuery(id+"F0.wireOp",EDGE,"E103"),sQuery(id+"F0.wireOp",EDGE,"E104"),sQuery(id+"F0.wireOp",EDGE,"E105"),sQuery(id+"F0.wireOp",EDGE,"E106"),sQuery(id+"F0.wireOp",EDGE,"E107"),sQuery(id+"F0.wireOp",EDGE,"E108"),sQuery(id+"F0.wireOp",EDGE,"E109"),sQuery(id+"F0.wireOp",EDGE,"E110"),sQuery(id+"F0.wireOp",EDGE,"E111"),sQuery(id+"F0.wireOp",EDGE,"E112"),sQuery(id+"F0.wireOp",EDGE,"E113"),sQuery(id+"F0.wireOp",EDGE,"E114"),sQuery(id+"F0.wireOp",EDGE,"E115"),sQuery(id+"F0.wireOp",EDGE,"E116"),sQuery(id+"F0.wireOp",EDGE,"E117"),sQuery(id+"F0.wireOp",EDGE,"E118"),sQuery(id+"F0.wireOp",EDGE,"E119"),sQuery(id+"F0.wireOp",EDGE,"E120"),sQuery(id+"F0.wireOp",EDGE,"E121"),sQuery(id+"F0.wireOp",EDGE,"E122"),sQuery(id+"F0.wireOp",EDGE,"E123"),sQuery(id+"F0.wireOp",EDGE,"E124"),sQuery(id+"F0.wireOp",EDGE,"E125"),sQuery(id+"F0.wireOp",EDGE,"E126"),sQuery(id+"F0.wireOp",EDGE,"E127"),sQuery(id+"F0.wireOp",EDGE,"E130"),sQuery(id+"F0.wireOp",EDGE,"wEKJqsZE-Lnf2-Pc3B-vstB-3JEagEBnImep"),sQuery(id+"F0.wireOp",EDGE,"E133"),sQuery(id+"F0.wireOp",EDGE,"E137"),sQuery(id+"F0.wireOp",EDGE,"E141"),sQuery(id+"F0.wireOp",EDGE,"E142"),sQuery(id+"F0.wireOp",EDGE,"E151"),sQuery(id+"F0.wireOp",EDGE,"E152"),sQuery(id+"F0.wireOp",EDGE,"XqZMZlJO-xrwS-6yc9-YKlE-u4GM9skw6DG2"),sQuery(id+"F0.wireOp",EDGE,"E153"),sQuery(id+"F0.wireOp",EDGE,"E154"),sQuery(id+"F0.wireOp",EDGE,"MRLSVep9-wh13-aC8x-J69K-2GoYUCsBfXyJ"),sQuery(id+"F0.wireOp",EDGE,"E155")])],"isStart":false});
            var sketch = newSketch(context, id + "F17", { "sketchPlane" : qUnion([Q0])});
            skSolve(sketch);
        }
        {
            var Q0;
            Q0=makeQuery(id+"F1.opExtrude","SWEPT_FACE",FACE,{"disambiguationData":[OSD([sQuery(id+"F0.wireOp",EDGE,"E12")])]});
            var sketch = newSketch(context, id + "F18", { "sketchPlane" : qUnion([Q0])});
            skLineSegment(sketch, "E213", {"start": v(1218.11, 254) * mm, "end": v(1268.91, 254) * mm});
            skLineSegment(sketch, "E214", {"start": v(1268.91, 254) * mm, "end": v(1675.31, 254) * mm});
            skLineSegment(sketch, "E215", {"start": v(1675.31, 254) * mm, "end": v(1730.4, 254) * mm});
            skLineSegment(sketch, "E216", {"start": v(1730.4, 254) * mm, "end": v(2009.8, 254) * mm});
            skLineSegment(sketch, "E217", {"start": v(2009.8, 254) * mm, "end": v(2589.71, 254) * mm});
            skLineSegment(sketch, "E218", {"start": v(1472.11, 254) * mm, "end": v(1472.11, 203.2) * mm});
            skLineSegment(sketch, "E219", {"start": v(1472.11, 203.2) * mm, "end": v(1370.51, 203.2) * mm});
            skLineSegment(sketch, "E220", {"start": v(1370.51, 203.2) * mm, "end": v(1370.51, 101.6) * mm});
            skLineSegment(sketch, "E221", {"start": v(1370.51, 101.6) * mm, "end": v(1573.71, 101.6) * mm});
            skLineSegment(sketch, "E222", {"start": v(1573.71, 101.6) * mm, "end": v(1573.71, 203.2) * mm});
            skLineSegment(sketch, "E223", {"start": v(1573.71, 203.2) * mm, "end": v(1472.11, 203.2) * mm});
            skLineSegment(sketch, "E224", {"start": v(2299.75, 254) * mm, "end": v(2299.75, 203.2) * mm});
            skLineSegment(sketch, "E225", {"start": v(2299.75, 203.2) * mm, "end": v(2147.35, 203.2) * mm});
            skLineSegment(sketch, "E226", {"start": v(2147.35, 203.2) * mm, "end": v(2147.35, 101.6) * mm});
            skLineSegment(sketch, "E227", {"start": v(2147.35, 101.6) * mm, "end": v(2452.15, 101.6) * mm});
            skLineSegment(sketch, "E228", {"start": v(2452.15, 101.6) * mm, "end": v(2452.15, 203.2) * mm});
            skLineSegment(sketch, "E229", {"start": v(2452.15, 203.2) * mm, "end": v(2299.75, 203.2) * mm});
            skSolve(sketch);
        }
        {
            var Q0;
            Q0 = qSketchRegion(id + "F18", true);
            extrude(context, id + "F19", {"entities" : qUnion([Q0]), "operationType" : NewBodyOperationType.REMOVE, "oppositeDirection" : true, "depth" : 76.2 * mm, "offsetDistance" : 25.4 * mm});
        }
        {
            var Q0;
            Q0=makeQuery(id+"F1.opExtrude","SWEPT_FACE",FACE,{"disambiguationData":[OSD([sQuery(id+"F0.wireOp",EDGE,"E13"),sQuery(id+"F0.wireOp",EDGE,"E106"),sQuery(id+"F0.wireOp",EDGE,"E108"),sQuery(id+"F0.wireOp",EDGE,"E125")])]});
            var sketch = newSketch(context, id + "F20", { "sketchPlane" : qUnion([Q0])});
            skLineSegment(sketch, "E230", {"start": v(-2136.53, 254) * mm, "end": v(-2085.73, 254) * mm});
            skLineSegment(sketch, "E231", {"start": v(-2085.73, 254) * mm, "end": v(-1399.93, 254) * mm});
            skLineSegment(sketch, "E232", {"start": v(-1399.93, 254) * mm, "end": v(-1349.13, 254) * mm});
            skLineSegment(sketch, "E233", {"start": v(-1742.83, 254) * mm, "end": v(-1742.83, 203.2) * mm});
            skLineSegment(sketch, "E234", {"start": v(-1742.83, 203.2) * mm, "end": v(-1920.63, 203.2) * mm});
            skLineSegment(sketch, "E235", {"start": v(-1920.63, 203.2) * mm, "end": v(-1920.63, 76.2) * mm});
            skLineSegment(sketch, "E236", {"start": v(-1920.63, 76.2) * mm, "end": v(-1565.03, 76.2) * mm});
            skLineSegment(sketch, "E237", {"start": v(-1565.03, 76.2) * mm, "end": v(-1565.03, 203.2) * mm});
            skLineSegment(sketch, "E238", {"start": v(-1565.03, 203.2) * mm, "end": v(-1742.83, 203.2) * mm});
            skSolve(sketch);
        }
        {
            var Q0;
            Q0 = qSketchRegion(id + "F20", true);
            extrude(context, id + "F21", {"entities" : qUnion([Q0]), "operationType" : NewBodyOperationType.REMOVE, "oppositeDirection" : true, "depth" : 76.2 * mm, "offsetDistance" : 25.4 * mm});
        }
        {
            var Q0;
            Q0=makeQuery(id+"F1.opExtrude","SWEPT_FACE",FACE,{"disambiguationData":[OSD([sQuery(id+"F0.wireOp",EDGE,"E13"),sQuery(id+"F0.wireOp",EDGE,"E106"),sQuery(id+"F0.wireOp",EDGE,"E108"),sQuery(id+"F0.wireOp",EDGE,"E125")])]});
            var sketch = newSketch(context, id + "F22", { "sketchPlane" : qUnion([Q0])});
            skLineSegment(sketch, "E239", {"start": v(-231.53, 254) * mm, "end": v(-282.33, 254) * mm});
            skLineSegment(sketch, "E240", {"start": v(-282.33, 254) * mm, "end": v(-1323.73, 254) * mm});
            skLineSegment(sketch, "E241", {"start": v(-803.03, 254) * mm, "end": v(-803.03, 203.2) * mm});
            skPoint(sketch, "E241.endSnap0", {"position": v(-803.03, 254) * mm});
            skLineSegment(sketch, "E242", {"start": v(-803.03, 203.2) * mm, "end": v(-1285.63, 203.2) * mm});
            skLineSegment(sketch, "E243", {"start": v(-1285.63, 203.2) * mm, "end": v(-1285.63, 25.4) * mm});
            skLineSegment(sketch, "E244", {"start": v(-1285.63, 25.4) * mm, "end": v(-320.43, 25.4) * mm});
            skLineSegment(sketch, "E245", {"start": v(-320.43, 25.4) * mm, "end": v(-320.43, 203.2) * mm});
            skLineSegment(sketch, "E246", {"start": v(-320.43, 203.2) * mm, "end": v(-803.03, 203.2) * mm});
            skSolve(sketch);
        }
        {
            var Q0;
            Q0 = qSketchRegion(id + "F22", true);
            extrude(context, id + "F23", {"entities" : qUnion([Q0]), "operationType" : NewBodyOperationType.REMOVE, "oppositeDirection" : true, "depth" : 76.2 * mm, "offsetDistance" : 25.4 * mm});
        }
        {
            var Q0;
            Q0=makeQuery(id+"F1.opExtrude","SWEPT_FACE",FACE,{"disambiguationData":[OSD([sQuery(id+"F0.wireOp",EDGE,"E22"),sQuery(id+"F0.wireOp",EDGE,"E107")])]});
            var sketch = newSketch(context, id + "F24", { "sketchPlane" : qUnion([Q0])});
            skLineSegment(sketch, "E247", {"start": v(-2589.71, 254) * mm, "end": v(-2538.91, 254) * mm});
            skLineSegment(sketch, "E248", {"start": v(-2538.91, 203.2) * mm, "end": v(-2538.91, 25.4) * mm});
            skLineSegment(sketch, "E249", {"start": v(-2538.91, 254) * mm, "end": v(-2081.71, 254) * mm});
            skLineSegment(sketch, "E250", {"start": v(-2081.71, 25.4) * mm, "end": v(-2538.91, 25.4) * mm});
            skLineSegment(sketch, "E251", {"start": v(-2081.71, 25.4) * mm, "end": v(-2081.71, 203.2) * mm});
            skLineSegment(sketch, "E252", {"start": v(-2081.71, 203.2) * mm, "end": v(-2538.91, 203.2) * mm});
            skSolve(sketch);
        }
        {
            var Q0;
            Q0 = qSketchRegion(id + "F24", true);
            extrude(context, id + "F25", {"entities" : qUnion([Q0]), "operationType" : NewBodyOperationType.REMOVE, "oppositeDirection" : true, "depth" : 76.2 * mm, "offsetDistance" : 25.4 * mm});
        }
        {
            var Q0;
            Q0=makeQuery(id+"F1.opExtrude","SWEPT_FACE",FACE,{"disambiguationData":[OSD([sQuery(id+"F0.wireOp",EDGE,"E22"),sQuery(id+"F0.wireOp",EDGE,"E107")])]});
            var sketch = newSketch(context, id + "F26", { "sketchPlane" : qUnion([Q0])});
            skLineSegment(sketch, "E253", {"start": v(-2081.71, 203.2) * mm, "end": v(-1980.11, 203.2) * mm});
            skLineSegment(sketch, "E254", {"start": v(-1980.11, 203.2) * mm, "end": v(-1294.31, 203.2) * mm});
            skLineSegment(sketch, "E255", {"start": v(-1637.21, 76.2) * mm, "end": v(-1764.21, 76.2) * mm});
            skLineSegment(sketch, "E256", {"start": v(-1764.21, 76.2) * mm, "end": v(-1764.21, 203.2) * mm});
            skLineSegment(sketch, "E257", {"start": v(-1764.21, 203.2) * mm, "end": v(-1510.21, 203.2) * mm});
            skLineSegment(sketch, "E258", {"start": v(-1510.21, 203.2) * mm, "end": v(-1510.21, 76.2) * mm});
            skLineSegment(sketch, "E259", {"start": v(-1510.21, 76.2) * mm, "end": v(-1637.21, 76.2) * mm});
            skSolve(sketch);
        }
        {
            var Q0;
            Q0 = qSketchRegion(id + "F26", true);
            extrude(context, id + "F27", {"entities" : qUnion([Q0]), "operationType" : NewBodyOperationType.REMOVE, "oppositeDirection" : true, "depth" : 76.2 * mm, "offsetDistance" : 25.4 * mm});
        }
        {
            var Q0;
            Q0=makeQuery(id+"F1.opExtrude","SWEPT_FACE",FACE,{"disambiguationData":[OSD([sQuery(id+"F0.wireOp",EDGE,"E22"),sQuery(id+"F0.wireOp",EDGE,"E107")])]});
            var sketch = newSketch(context, id + "F28", { "sketchPlane" : qUnion([Q0])});
            skLineSegment(sketch, "E260", {"start": v(-2538.91, 203.2) * mm, "end": v(-2081.71, 203.2) * mm});
            skLineSegment(sketch, "E261", {"start": v(-2310.31, 25.4) * mm, "end": v(-2361.11, 25.4) * mm});
            skLineSegment(sketch, "E262", {"start": v(-2361.11, 25.4) * mm, "end": v(-2361.11, 203.2) * mm});
            skLineSegment(sketch, "E263", {"start": v(-2361.11, 203.2) * mm, "end": v(-2310.31, 203.2) * mm});
            skLineSegment(sketch, "E264", {"start": v(-2310.31, 203.2) * mm, "end": v(-2259.51, 203.2) * mm});
            skLineSegment(sketch, "E265", {"start": v(-2259.51, 203.2) * mm, "end": v(-2259.51, 25.4) * mm});
            skLineSegment(sketch, "E266", {"start": v(-2259.51, 25.4) * mm, "end": v(-2310.31, 25.4) * mm});
            skLineSegment(sketch, "E267", {"start": v(-2361.11, 203.2) * mm, "end": v(-2361.11, 254) * mm});
            skLineSegment(sketch, "E268", {"start": v(-2361.11, 254) * mm, "end": v(-2259.51, 254) * mm});
            skLineSegment(sketch, "E269", {"start": v(-2259.51, 254) * mm, "end": v(-2259.51, 203.2) * mm});
            skLineSegment(sketch, "E270", {"start": v(-2361.11, 254) * mm, "end": v(-2386.51, 254) * mm});
            skLineSegment(sketch, "E271", {"start": v(-2386.51, 254) * mm, "end": v(-2386.51, 0) * mm});
            skLineSegment(sketch, "E272", {"start": v(-2386.51, 0) * mm, "end": v(-2259.51, 0) * mm});
            skLineSegment(sketch, "E273", {"start": v(-2259.51, 0) * mm, "end": v(-2259.51, 25.4) * mm});
            skLineSegment(sketch, "E274", {"start": v(-2259.51, 0) * mm, "end": v(-2234.11, 0) * mm});
            skLineSegment(sketch, "E275", {"start": v(-2234.11, 0) * mm, "end": v(-2234.11, 254) * mm});
            skLineSegment(sketch, "E276", {"start": v(-2234.11, 254) * mm, "end": v(-2259.51, 254) * mm});
            skLineSegment(sketch, "E277", {"start": v(-2386.51, 254) * mm, "end": v(-2234.11, 254) * mm});
            skSolve(sketch);
        }
        {
            var Q0;
            Q0 = qSketchRegion(id + "F28", true);
            extrude(context, id + "F29", {"entities" : qUnion([Q0]), "oppositeDirection" : true, "depth" : 50.8 * mm, "offsetDistance" : 25.4 * mm});
        }
        {
            var Q0;
            Q0=makeQuery(id+"F1.opExtrude","CAP_FACE",FACE,{"disambiguationData":[OSD([sQuery(id+"F0.wireOp",EDGE,"E0"),sQuery(id+"F0.wireOp",EDGE,"E1"),sQuery(id+"F0.wireOp",EDGE,"E2"),sQuery(id+"F0.wireOp",EDGE,"E3"),sQuery(id+"F0.wireOp",EDGE,"E4"),sQuery(id+"F0.wireOp",EDGE,"E5"),sQuery(id+"F0.wireOp",EDGE,"E6"),sQuery(id+"F0.wireOp",EDGE,"E7"),sQuery(id+"F0.wireOp",EDGE,"E8"),sQuery(id+"F0.wireOp",EDGE,"E9"),sQuery(id+"F0.wireOp",EDGE,"E10"),sQuery(id+"F0.wireOp",EDGE,"E11"),sQuery(id+"F0.wireOp",EDGE,"E12"),sQuery(id+"F0.wireOp",EDGE,"E13"),sQuery(id+"F0.wireOp",EDGE,"E14"),sQuery(id+"F0.wireOp",EDGE,"E15"),sQuery(id+"F0.wireOp",EDGE,"E16"),sQuery(id+"F0.wireOp",EDGE,"E17"),sQuery(id+"F0.wireOp",EDGE,"E18"),sQuery(id+"F0.wireOp",EDGE,"E19"),sQuery(id+"F0.wireOp",EDGE,"E20"),sQuery(id+"F0.wireOp",EDGE,"E21"),sQuery(id+"F0.wireOp",EDGE,"E22"),sQuery(id+"F0.wireOp",EDGE,"E23"),sQuery(id+"F0.wireOp",EDGE,"E24"),sQuery(id+"F0.wireOp",EDGE,"E25"),sQuery(id+"F0.wireOp",EDGE,"E26"),sQuery(id+"F0.wireOp",EDGE,"E27"),sQuery(id+"F0.wireOp",EDGE,"E28"),sQuery(id+"F0.wireOp",EDGE,"E29"),sQuery(id+"F0.wireOp",EDGE,"E30"),sQuery(id+"F0.wireOp",EDGE,"E31"),sQuery(id+"F0.wireOp",EDGE,"E32"),sQuery(id+"F0.wireOp",EDGE,"E34"),sQuery(id+"F0.wireOp",EDGE,"E35"),sQuery(id+"F0.wireOp",EDGE,"E36"),sQuery(id+"F0.wireOp",EDGE,"E37"),sQuery(id+"F0.wireOp",EDGE,"E38"),sQuery(id+"F0.wireOp",EDGE,"E39"),sQuery(id+"F0.wireOp",EDGE,"E40"),sQuery(id+"F0.wireOp",EDGE,"E41"),sQuery(id+"F0.wireOp",EDGE,"E42"),sQuery(id+"F0.wireOp",EDGE,"E43"),sQuery(id+"F0.wireOp",EDGE,"E44"),sQuery(id+"F0.wireOp",EDGE,"E45"),sQuery(id+"F0.wireOp",EDGE,"E46"),sQuery(id+"F0.wireOp",EDGE,"E47"),sQuery(id+"F0.wireOp",EDGE,"E48"),sQuery(id+"F0.wireOp",EDGE,"E49"),sQuery(id+"F0.wireOp",EDGE,"E50"),sQuery(id+"F0.wireOp",EDGE,"E51"),sQuery(id+"F0.wireOp",EDGE,"E52"),sQuery(id+"F0.wireOp",EDGE,"E53"),sQuery(id+"F0.wireOp",EDGE,"E54"),sQuery(id+"F0.wireOp",EDGE,"E55"),sQuery(id+"F0.wireOp",EDGE,"E56"),sQuery(id+"F0.wireOp",EDGE,"E57"),sQuery(id+"F0.wireOp",EDGE,"E58"),sQuery(id+"F0.wireOp",EDGE,"E59"),sQuery(id+"F0.wireOp",EDGE,"E60"),sQuery(id+"F0.wireOp",EDGE,"E61"),sQuery(id+"F0.wireOp",EDGE,"E62"),sQuery(id+"F0.wireOp",EDGE,"E63"),sQuery(id+"F0.wireOp",EDGE,"E64"),sQuery(id+"F0.wireOp",EDGE,"E65"),sQuery(id+"F0.wireOp",EDGE,"E66"),sQuery(id+"F0.wireOp",EDGE,"E67"),sQuery(id+"F0.wireOp",EDGE,"E68"),sQuery(id+"F0.wireOp",EDGE,"E69"),sQuery(id+"F0.wireOp",EDGE,"E70"),sQuery(id+"F0.wireOp",EDGE,"E71"),sQuery(id+"F0.wireOp",EDGE,"E72"),sQuery(id+"F0.wireOp",EDGE,"E73"),sQuery(id+"F0.wireOp",EDGE,"E74"),sQuery(id+"F0.wireOp",EDGE,"E75"),sQuery(id+"F0.wireOp",EDGE,"E76"),sQuery(id+"F0.wireOp",EDGE,"E77"),sQuery(id+"F0.wireOp",EDGE,"E78"),sQuery(id+"F0.wireOp",EDGE,"E79"),sQuery(id+"F0.wireOp",EDGE,"E80"),sQuery(id+"F0.wireOp",EDGE,"E81"),sQuery(id+"F0.wireOp",EDGE,"E82"),sQuery(id+"F0.wireOp",EDGE,"E83"),sQuery(id+"F0.wireOp",EDGE,"E84"),sQuery(id+"F0.wireOp",EDGE,"E85"),sQuery(id+"F0.wireOp",EDGE,"E86"),sQuery(id+"F0.wireOp",EDGE,"E87"),sQuery(id+"F0.wireOp",EDGE,"E88"),sQuery(id+"F0.wireOp",EDGE,"E89"),sQuery(id+"F0.wireOp",EDGE,"E90"),sQuery(id+"F0.wireOp",EDGE,"E91"),sQuery(id+"F0.wireOp",EDGE,"E92"),sQuery(id+"F0.wireOp",EDGE,"E93"),sQuery(id+"F0.wireOp",EDGE,"E94"),sQuery(id+"F0.wireOp",EDGE,"E95"),sQuery(id+"F0.wireOp",EDGE,"E96"),sQuery(id+"F0.wireOp",EDGE,"E97"),sQuery(id+"F0.wireOp",EDGE,"E98"),sQuery(id+"F0.wireOp",EDGE,"E99"),sQuery(id+"F0.wireOp",EDGE,"E100"),sQuery(id+"F0.wireOp",EDGE,"E101"),sQuery(id+"F0.wireOp",EDGE,"E102"),sQuery(id+"F0.wireOp",EDGE,"E103"),sQuery(id+"F0.wireOp",EDGE,"E104"),sQuery(id+"F0.wireOp",EDGE,"E105"),sQuery(id+"F0.wireOp",EDGE,"E106"),sQuery(id+"F0.wireOp",EDGE,"E107"),sQuery(id+"F0.wireOp",EDGE,"E108"),sQuery(id+"F0.wireOp",EDGE,"E109"),sQuery(id+"F0.wireOp",EDGE,"E110"),sQuery(id+"F0.wireOp",EDGE,"E111"),sQuery(id+"F0.wireOp",EDGE,"E112"),sQuery(id+"F0.wireOp",EDGE,"E113"),sQuery(id+"F0.wireOp",EDGE,"E114"),sQuery(id+"F0.wireOp",EDGE,"E115"),sQuery(id+"F0.wireOp",EDGE,"E116"),sQuery(id+"F0.wireOp",EDGE,"E117"),sQuery(id+"F0.wireOp",EDGE,"E118"),sQuery(id+"F0.wireOp",EDGE,"E119"),sQuery(id+"F0.wireOp",EDGE,"E120"),sQuery(id+"F0.wireOp",EDGE,"E121"),sQuery(id+"F0.wireOp",EDGE,"E122"),sQuery(id+"F0.wireOp",EDGE,"E123"),sQuery(id+"F0.wireOp",EDGE,"E124"),sQuery(id+"F0.wireOp",EDGE,"E125"),sQuery(id+"F0.wireOp",EDGE,"E126"),sQuery(id+"F0.wireOp",EDGE,"E127"),sQuery(id+"F0.wireOp",EDGE,"E128"),sQuery(id+"F0.wireOp",EDGE,"E129"),sQuery(id+"F0.wireOp",EDGE,"E130"),sQuery(id+"F0.wireOp",EDGE,"E131"),sQuery(id+"F0.wireOp",EDGE,"E132"),sQuery(id+"F0.wireOp",EDGE,"E133"),sQuery(id+"F0.wireOp",EDGE,"E137"),sQuery(id+"F0.wireOp",EDGE,"E141"),sQuery(id+"F0.wireOp",EDGE,"E142"),sQuery(id+"F0.wireOp",EDGE,"E143"),sQuery(id+"F0.wireOp",EDGE,"E146"),sQuery(id+"F0.wireOp",EDGE,"E147"),sQuery(id+"F0.wireOp",EDGE,"E148"),sQuery(id+"F0.wireOp",EDGE,"E151"),sQuery(id+"F0.wireOp",EDGE,"E152"),sQuery(id+"F0.wireOp",EDGE,"E153"),sQuery(id+"F0.wireOp",EDGE,"E154"),sQuery(id+"F0.wireOp",EDGE,"E155"),sQuery(id+"F0.wireOp",EDGE,"E156"),sQuery(id+"F0.wireOp",EDGE,"E157"),sQuery(id+"F0.wireOp",EDGE,"E158"),sQuery(id+"F0.wireOp",EDGE,"E159"),sQuery(id+"F0.wireOp",EDGE,"E160"),sQuery(id+"F0.wireOp",EDGE,"E161"),sQuery(id+"F0.wireOp",EDGE,"E162"),sQuery(id+"F0.wireOp",EDGE,"E163"),sQuery(id+"F0.wireOp",EDGE,"E164"),sQuery(id+"F0.wireOp",EDGE,"E165"),sQuery(id+"F0.wireOp",EDGE,"E166"),sQuery(id+"F0.wireOp",EDGE,"E167"),sQuery(id+"F0.wireOp",EDGE,"E168")])],"isStart":true});
            var sketch = newSketch(context, id + "F30", { "sketchPlane" : qUnion([Q0])});
            skLineSegment(sketch, "E278.bottom", {"start": v(-1104.75, 597.15) * mm, "end": v(2950.43, 597.15) * mm});
            skLineSegment(sketch, "E278.top", {"start": v(-1104.75, -3137.36) * mm, "end": v(2950.43, -3137.36) * mm});
            skLineSegment(sketch, "E278.left", {"start": v(-1104.75, 597.15) * mm, "end": v(-1104.75, -3137.36) * mm});
            skLineSegment(sketch, "E278.right", {"start": v(2950.43, 597.15) * mm, "end": v(2950.43, -3137.36) * mm});
            skSolve(sketch);
        }
        {
            var Q0;
            Q0=makeQuery(id+"F30.imprint","IMPRINT",FACE,{"disambiguationData":[TD([[makeQuery(id+"F30.imprint","IMPRINT",EDGE,{"derivedFrom":sQuery(id+"F30.wireOp",EDGE,"E278.bottom")}),-1.0]])]});
            var Q1;
            Q1=makeQuery(id+"F30.imprint","IMPRINT",FACE,{"disambiguationData":[TD([[makeQuery(id+"F30.imprint","IMPRINT",EDGE,{"derivedFrom":makeQuery(id+"F1.opExtrude","CAP_EDGE",EDGE,{"disambiguationData":[OSD([sQuery(id+"F0.wireOp",EDGE,"E16")])],"isStart":true})}),-1.0]])]});
            extrude(context, id + "F31", {"entities" : qUnion([Q0, Q1]), "depth" : 50.8 * mm, "offsetDistance" : 25.4 * mm});
        }
        {
            var Q0;
            Q0=makeQuery(id+"F31.opExtrude","CAP_FACE",FACE,{"disambiguationData":[OSD([sQuery(id+"F0.wireOp",EDGE,"E1"),sQuery(id+"F0.wireOp",EDGE,"E2"),sQuery(id+"F0.wireOp",EDGE,"E3"),sQuery(id+"F0.wireOp",EDGE,"E4"),sQuery(id+"F0.wireOp",EDGE,"E6"),sQuery(id+"F0.wireOp",EDGE,"E7"),sQuery(id+"F0.wireOp",EDGE,"E8"),sQuery(id+"F0.wireOp",EDGE,"E9"),sQuery(id+"F0.wireOp",EDGE,"E10"),sQuery(id+"F0.wireOp",EDGE,"E11"),sQuery(id+"F0.wireOp",EDGE,"E12"),sQuery(id+"F0.wireOp",EDGE,"E13"),sQuery(id+"F0.wireOp",EDGE,"E19"),sQuery(id+"F0.wireOp",EDGE,"E20"),sQuery(id+"F0.wireOp",EDGE,"E21"),sQuery(id+"F0.wireOp",EDGE,"E22"),sQuery(id+"F0.wireOp",EDGE,"E24"),sQuery(id+"F0.wireOp",EDGE,"E25"),sQuery(id+"F0.wireOp",EDGE,"E26"),sQuery(id+"F0.wireOp",EDGE,"E27"),sQuery(id+"F0.wireOp",EDGE,"E28"),sQuery(id+"F0.wireOp",EDGE,"E29"),sQuery(id+"F0.wireOp",EDGE,"E30"),sQuery(id+"F0.wireOp",EDGE,"E31"),sQuery(id+"F0.wireOp",EDGE,"E32"),sQuery(id+"F0.wireOp",EDGE,"E34"),sQuery(id+"F0.wireOp",EDGE,"E35"),sQuery(id+"F0.wireOp",EDGE,"E36"),sQuery(id+"F0.wireOp",EDGE,"E37"),sQuery(id+"F0.wireOp",EDGE,"E38"),sQuery(id+"F0.wireOp",EDGE,"E39"),sQuery(id+"F0.wireOp",EDGE,"E40"),sQuery(id+"F0.wireOp",EDGE,"E41"),sQuery(id+"F0.wireOp",EDGE,"E42"),sQuery(id+"F0.wireOp",EDGE,"E43"),sQuery(id+"F0.wireOp",EDGE,"E44"),sQuery(id+"F0.wireOp",EDGE,"E45"),sQuery(id+"F0.wireOp",EDGE,"E46"),sQuery(id+"F0.wireOp",EDGE,"E47"),sQuery(id+"F0.wireOp",EDGE,"E48"),sQuery(id+"F0.wireOp",EDGE,"E49"),sQuery(id+"F0.wireOp",EDGE,"E50"),sQuery(id+"F0.wireOp",EDGE,"E51"),sQuery(id+"F0.wireOp",EDGE,"E52"),sQuery(id+"F0.wireOp",EDGE,"E53"),sQuery(id+"F0.wireOp",EDGE,"E54"),sQuery(id+"F0.wireOp",EDGE,"E55"),sQuery(id+"F0.wireOp",EDGE,"E56"),sQuery(id+"F0.wireOp",EDGE,"E57"),sQuery(id+"F0.wireOp",EDGE,"E58"),sQuery(id+"F0.wireOp",EDGE,"E59"),sQuery(id+"F0.wireOp",EDGE,"E60"),sQuery(id+"F0.wireOp",EDGE,"E61"),sQuery(id+"F0.wireOp",EDGE,"E62"),sQuery(id+"F0.wireOp",EDGE,"E63"),sQuery(id+"F0.wireOp",EDGE,"E64"),sQuery(id+"F0.wireOp",EDGE,"E65"),sQuery(id+"F0.wireOp",EDGE,"E66"),sQuery(id+"F0.wireOp",EDGE,"E67"),sQuery(id+"F0.wireOp",EDGE,"E68"),sQuery(id+"F0.wireOp",EDGE,"E69"),sQuery(id+"F0.wireOp",EDGE,"E70"),sQuery(id+"F0.wireOp",EDGE,"E71"),sQuery(id+"F0.wireOp",EDGE,"E72"),sQuery(id+"F0.wireOp",EDGE,"E73"),sQuery(id+"F0.wireOp",EDGE,"E74"),sQuery(id+"F0.wireOp",EDGE,"E75"),sQuery(id+"F0.wireOp",EDGE,"E76"),sQuery(id+"F0.wireOp",EDGE,"E77"),sQuery(id+"F0.wireOp",EDGE,"E78"),sQuery(id+"F0.wireOp",EDGE,"E79"),sQuery(id+"F0.wireOp",EDGE,"E80"),sQuery(id+"F0.wireOp",EDGE,"E81"),sQuery(id+"F0.wireOp",EDGE,"E82"),sQuery(id+"F0.wireOp",EDGE,"E83"),sQuery(id+"F0.wireOp",EDGE,"E84"),sQuery(id+"F0.wireOp",EDGE,"E85"),sQuery(id+"F0.wireOp",EDGE,"E86"),sQuery(id+"F0.wireOp",EDGE,"E87"),sQuery(id+"F0.wireOp",EDGE,"E88"),sQuery(id+"F0.wireOp",EDGE,"E89"),sQuery(id+"F0.wireOp",EDGE,"E90"),sQuery(id+"F0.wireOp",EDGE,"E91"),sQuery(id+"F0.wireOp",EDGE,"E94"),sQuery(id+"F0.wireOp",EDGE,"E95"),sQuery(id+"F0.wireOp",EDGE,"E98"),sQuery(id+"F0.wireOp",EDGE,"E99"),sQuery(id+"F0.wireOp",EDGE,"E100"),sQuery(id+"F0.wireOp",EDGE,"E101"),sQuery(id+"F0.wireOp",EDGE,"E102"),sQuery(id+"F0.wireOp",EDGE,"E103"),sQuery(id+"F0.wireOp",EDGE,"E104"),sQuery(id+"F0.wireOp",EDGE,"E105"),sQuery(id+"F0.wireOp",EDGE,"E106"),sQuery(id+"F0.wireOp",EDGE,"E107"),sQuery(id+"F0.wireOp",EDGE,"E108"),sQuery(id+"F0.wireOp",EDGE,"E109"),sQuery(id+"F0.wireOp",EDGE,"E110"),sQuery(id+"F0.wireOp",EDGE,"E111"),sQuery(id+"F0.wireOp",EDGE,"E112"),sQuery(id+"F0.wireOp",EDGE,"E113"),sQuery(id+"F0.wireOp",EDGE,"E114"),sQuery(id+"F0.wireOp",EDGE,"E115"),sQuery(id+"F0.wireOp",EDGE,"E116"),sQuery(id+"F0.wireOp",EDGE,"E117"),sQuery(id+"F0.wireOp",EDGE,"E118"),sQuery(id+"F0.wireOp",EDGE,"E119"),sQuery(id+"F0.wireOp",EDGE,"E120"),sQuery(id+"F0.wireOp",EDGE,"E121"),sQuery(id+"F0.wireOp",EDGE,"E122"),sQuery(id+"F0.wireOp",EDGE,"E123"),sQuery(id+"F0.wireOp",EDGE,"E124"),sQuery(id+"F0.wireOp",EDGE,"E125"),sQuery(id+"F0.wireOp",EDGE,"E126"),sQuery(id+"F0.wireOp",EDGE,"E127"),sQuery(id+"F0.wireOp",EDGE,"E128"),sQuery(id+"F0.wireOp",EDGE,"E129"),sQuery(id+"F0.wireOp",EDGE,"E130"),sQuery(id+"F0.wireOp",EDGE,"E131"),sQuery(id+"F0.wireOp",EDGE,"E132"),sQuery(id+"F0.wireOp",EDGE,"E133"),sQuery(id+"F0.wireOp",EDGE,"E137"),sQuery(id+"F0.wireOp",EDGE,"E141"),sQuery(id+"F0.wireOp",EDGE,"E142"),sQuery(id+"F0.wireOp",EDGE,"E143"),sQuery(id+"F0.wireOp",EDGE,"E146"),sQuery(id+"F0.wireOp",EDGE,"E147"),sQuery(id+"F0.wireOp",EDGE,"E148"),sQuery(id+"F0.wireOp",EDGE,"E151"),sQuery(id+"F0.wireOp",EDGE,"E152"),sQuery(id+"F0.wireOp",EDGE,"E153"),sQuery(id+"F0.wireOp",EDGE,"E154"),sQuery(id+"F0.wireOp",EDGE,"E155"),sQuery(id+"F0.wireOp",EDGE,"E156"),sQuery(id+"F0.wireOp",EDGE,"E157"),sQuery(id+"F0.wireOp",EDGE,"E158"),sQuery(id+"F0.wireOp",EDGE,"E159"),sQuery(id+"F0.wireOp",EDGE,"E160"),sQuery(id+"F0.wireOp",EDGE,"E161"),sQuery(id+"F0.wireOp",EDGE,"E162"),sQuery(id+"F0.wireOp",EDGE,"E163"),sQuery(id+"F0.wireOp",EDGE,"E164"),sQuery(id+"F0.wireOp",EDGE,"E165"),sQuery(id+"F0.wireOp",EDGE,"E166"),sQuery(id+"F0.wireOp",EDGE,"E167"),sQuery(id+"F0.wireOp",EDGE,"E168"),sQuery(id+"F7.wireOp",EDGE,"E178"),sQuery(id+"F7.wireOp",EDGE,"E180"),sQuery(id+"F7.wireOp",EDGE,"E181"),sQuery(id+"F30.wireOp",EDGE,"E278.bottom"),sQuery(id+"F30.wireOp",EDGE,"E278.top"),sQuery(id+"F30.wireOp",EDGE,"E278.left"),sQuery(id+"F30.wireOp",EDGE,"E278.right")])],"isStart":true});
            var sketch = newSketch(context, id + "F32", { "sketchPlane" : qUnion([Q0])});
            skLineSegment(sketch, "E279", {"start": v(-1104.75, 3137.36) * mm, "end": v(-977.75, 3137.36) * mm});
            skLineSegment(sketch, "E280", {"start": v(-977.75, 3137.36) * mm, "end": v(-977.75, -672.64) * mm});
            skLineSegment(sketch, "E281", {"start": v(-977.75, -672.64) * mm, "end": v(2832.25, -672.64) * mm});
            skLineSegment(sketch, "E282", {"start": v(2832.25, -672.64) * mm, "end": v(2832.25, 2807.16) * mm});
            skLineSegment(sketch, "E283", {"start": v(2832.25, 2807.16) * mm, "end": v(-977.75, 2807.16) * mm});
            skLineSegment(sketch, "E284", {"start": v(-977.75, 3137.36) * mm, "end": v(2950.43, 3137.36) * mm});
            skLineSegment(sketch, "E285", {"start": v(2950.43, 3137.36) * mm, "end": v(2950.43, -597.15) * mm});
            skLineSegment(sketch, "E286", {"start": v(2950.43, -597.15) * mm, "end": v(-1104.75, -597.15) * mm});
            skLineSegment(sketch, "E287", {"start": v(-1104.75, -597.15) * mm, "end": v(-1104.75, 3137.36) * mm});
            skSolve(sketch);
        }
        {
            var Q0;
            {var subQ81=sQuery(id+"F32.wireOp",EDGE,"E281");Q0=makeQuery(id+"F32.imprint","IMPRINT",FACE,{"disambiguationData":[TD([[makeQuery(id+"F32.imprint","IMPRINT",EDGE,{"derivedFrom":subQ81}),1.0]])]});}
            var sketch = newSketch(context, id + "F33", { "sketchPlane" : qUnion([Q0])});
            skLineSegment(sketch, "E288", {"start": v(-762, 2419.47) * mm, "end": v(-762, 1403.47) * mm});
            skLineSegment(sketch, "E289", {"start": v(-762, 1403.47) * mm, "end": v(0, 1403.47) * mm});
            skLineSegment(sketch, "E290", {"start": v(0, 1403.47) * mm, "end": v(0, 2419.47) * mm});
            skLineSegment(sketch, "E291", {"start": v(0, 2419.47) * mm, "end": v(-762, 2419.47) * mm});
            skSolve(sketch);
        }
        {
            var Q0;
            Q0=makeQuery(id+"F33.imprint","IMPRINT",FACE,{"disambiguationData":[TD([[makeQuery(id+"F33.imprint","IMPRINT",EDGE,{"derivedFrom":sQuery(id+"F33.wireOp",EDGE,"E288")}),1.0]])]});
            extrude(context, id + "F34", {"entities" : qUnion([Q0]), "operationType" : NewBodyOperationType.REMOVE, "oppositeDirection" : true, "depth" : 76.2 * mm, "offsetDistance" : 25.4 * mm});
        }
        {
            var Q0;
            Q0=makeQuery(id+"F31.opExtrude","CAP_FACE",FACE,{"disambiguationData":[OSD([sQuery(id+"F0.wireOp",EDGE,"E1"),sQuery(id+"F0.wireOp",EDGE,"E2"),sQuery(id+"F0.wireOp",EDGE,"E3"),sQuery(id+"F0.wireOp",EDGE,"E4"),sQuery(id+"F0.wireOp",EDGE,"E6"),sQuery(id+"F0.wireOp",EDGE,"E7"),sQuery(id+"F0.wireOp",EDGE,"E8"),sQuery(id+"F0.wireOp",EDGE,"E9"),sQuery(id+"F0.wireOp",EDGE,"E10"),sQuery(id+"F0.wireOp",EDGE,"E11"),sQuery(id+"F0.wireOp",EDGE,"E12"),sQuery(id+"F0.wireOp",EDGE,"E13"),sQuery(id+"F0.wireOp",EDGE,"E19"),sQuery(id+"F0.wireOp",EDGE,"E20"),sQuery(id+"F0.wireOp",EDGE,"E21"),sQuery(id+"F0.wireOp",EDGE,"E22"),sQuery(id+"F0.wireOp",EDGE,"E24"),sQuery(id+"F0.wireOp",EDGE,"E25"),sQuery(id+"F0.wireOp",EDGE,"E26"),sQuery(id+"F0.wireOp",EDGE,"E27"),sQuery(id+"F0.wireOp",EDGE,"E28"),sQuery(id+"F0.wireOp",EDGE,"E29"),sQuery(id+"F0.wireOp",EDGE,"E30"),sQuery(id+"F0.wireOp",EDGE,"E31"),sQuery(id+"F0.wireOp",EDGE,"E32"),sQuery(id+"F0.wireOp",EDGE,"E34"),sQuery(id+"F0.wireOp",EDGE,"E35"),sQuery(id+"F0.wireOp",EDGE,"E36"),sQuery(id+"F0.wireOp",EDGE,"E37"),sQuery(id+"F0.wireOp",EDGE,"E38"),sQuery(id+"F0.wireOp",EDGE,"E39"),sQuery(id+"F0.wireOp",EDGE,"E40"),sQuery(id+"F0.wireOp",EDGE,"E41"),sQuery(id+"F0.wireOp",EDGE,"E42"),sQuery(id+"F0.wireOp",EDGE,"E43"),sQuery(id+"F0.wireOp",EDGE,"E44"),sQuery(id+"F0.wireOp",EDGE,"E45"),sQuery(id+"F0.wireOp",EDGE,"E46"),sQuery(id+"F0.wireOp",EDGE,"E47"),sQuery(id+"F0.wireOp",EDGE,"E48"),sQuery(id+"F0.wireOp",EDGE,"E49"),sQuery(id+"F0.wireOp",EDGE,"E50"),sQuery(id+"F0.wireOp",EDGE,"E51"),sQuery(id+"F0.wireOp",EDGE,"E52"),sQuery(id+"F0.wireOp",EDGE,"E53"),sQuery(id+"F0.wireOp",EDGE,"E54"),sQuery(id+"F0.wireOp",EDGE,"E55"),sQuery(id+"F0.wireOp",EDGE,"E56"),sQuery(id+"F0.wireOp",EDGE,"E57"),sQuery(id+"F0.wireOp",EDGE,"E58"),sQuery(id+"F0.wireOp",EDGE,"E59"),sQuery(id+"F0.wireOp",EDGE,"E60"),sQuery(id+"F0.wireOp",EDGE,"E61"),sQuery(id+"F0.wireOp",EDGE,"E62"),sQuery(id+"F0.wireOp",EDGE,"E63"),sQuery(id+"F0.wireOp",EDGE,"E64"),sQuery(id+"F0.wireOp",EDGE,"E65"),sQuery(id+"F0.wireOp",EDGE,"E66"),sQuery(id+"F0.wireOp",EDGE,"E67"),sQuery(id+"F0.wireOp",EDGE,"E68"),sQuery(id+"F0.wireOp",EDGE,"E69"),sQuery(id+"F0.wireOp",EDGE,"E70"),sQuery(id+"F0.wireOp",EDGE,"E71"),sQuery(id+"F0.wireOp",EDGE,"E72"),sQuery(id+"F0.wireOp",EDGE,"E73"),sQuery(id+"F0.wireOp",EDGE,"E74"),sQuery(id+"F0.wireOp",EDGE,"E75"),sQuery(id+"F0.wireOp",EDGE,"E76"),sQuery(id+"F0.wireOp",EDGE,"E77"),sQuery(id+"F0.wireOp",EDGE,"E78"),sQuery(id+"F0.wireOp",EDGE,"E79"),sQuery(id+"F0.wireOp",EDGE,"E80"),sQuery(id+"F0.wireOp",EDGE,"E81"),sQuery(id+"F0.wireOp",EDGE,"E82"),sQuery(id+"F0.wireOp",EDGE,"E83"),sQuery(id+"F0.wireOp",EDGE,"E84"),sQuery(id+"F0.wireOp",EDGE,"E85"),sQuery(id+"F0.wireOp",EDGE,"E86"),sQuery(id+"F0.wireOp",EDGE,"E87"),sQuery(id+"F0.wireOp",EDGE,"E88"),sQuery(id+"F0.wireOp",EDGE,"E89"),sQuery(id+"F0.wireOp",EDGE,"E90"),sQuery(id+"F0.wireOp",EDGE,"E91"),sQuery(id+"F0.wireOp",EDGE,"E94"),sQuery(id+"F0.wireOp",EDGE,"E95"),sQuery(id+"F0.wireOp",EDGE,"E98"),sQuery(id+"F0.wireOp",EDGE,"E99"),sQuery(id+"F0.wireOp",EDGE,"E100"),sQuery(id+"F0.wireOp",EDGE,"E101"),sQuery(id+"F0.wireOp",EDGE,"E102"),sQuery(id+"F0.wireOp",EDGE,"E103"),sQuery(id+"F0.wireOp",EDGE,"E104"),sQuery(id+"F0.wireOp",EDGE,"E105"),sQuery(id+"F0.wireOp",EDGE,"E106"),sQuery(id+"F0.wireOp",EDGE,"E107"),sQuery(id+"F0.wireOp",EDGE,"E108"),sQuery(id+"F0.wireOp",EDGE,"E109"),sQuery(id+"F0.wireOp",EDGE,"E110"),sQuery(id+"F0.wireOp",EDGE,"E111"),sQuery(id+"F0.wireOp",EDGE,"E112"),sQuery(id+"F0.wireOp",EDGE,"E113"),sQuery(id+"F0.wireOp",EDGE,"E114"),sQuery(id+"F0.wireOp",EDGE,"E115"),sQuery(id+"F0.wireOp",EDGE,"E116"),sQuery(id+"F0.wireOp",EDGE,"E117"),sQuery(id+"F0.wireOp",EDGE,"E118"),sQuery(id+"F0.wireOp",EDGE,"E119"),sQuery(id+"F0.wireOp",EDGE,"E120"),sQuery(id+"F0.wireOp",EDGE,"E121"),sQuery(id+"F0.wireOp",EDGE,"E122"),sQuery(id+"F0.wireOp",EDGE,"E123"),sQuery(id+"F0.wireOp",EDGE,"E124"),sQuery(id+"F0.wireOp",EDGE,"E125"),sQuery(id+"F0.wireOp",EDGE,"E126"),sQuery(id+"F0.wireOp",EDGE,"E127"),sQuery(id+"F0.wireOp",EDGE,"E128"),sQuery(id+"F0.wireOp",EDGE,"E129"),sQuery(id+"F0.wireOp",EDGE,"E130"),sQuery(id+"F0.wireOp",EDGE,"E131"),sQuery(id+"F0.wireOp",EDGE,"E132"),sQuery(id+"F0.wireOp",EDGE,"E133"),sQuery(id+"F0.wireOp",EDGE,"E137"),sQuery(id+"F0.wireOp",EDGE,"E141"),sQuery(id+"F0.wireOp",EDGE,"E142"),sQuery(id+"F0.wireOp",EDGE,"E143"),sQuery(id+"F0.wireOp",EDGE,"E146"),sQuery(id+"F0.wireOp",EDGE,"E147"),sQuery(id+"F0.wireOp",EDGE,"E148"),sQuery(id+"F0.wireOp",EDGE,"E151"),sQuery(id+"F0.wireOp",EDGE,"E152"),sQuery(id+"F0.wireOp",EDGE,"E153"),sQuery(id+"F0.wireOp",EDGE,"E154"),sQuery(id+"F0.wireOp",EDGE,"E155"),sQuery(id+"F0.wireOp",EDGE,"E156"),sQuery(id+"F0.wireOp",EDGE,"E157"),sQuery(id+"F0.wireOp",EDGE,"E158"),sQuery(id+"F0.wireOp",EDGE,"E159"),sQuery(id+"F0.wireOp",EDGE,"E160"),sQuery(id+"F0.wireOp",EDGE,"E161"),sQuery(id+"F0.wireOp",EDGE,"E162"),sQuery(id+"F0.wireOp",EDGE,"E163"),sQuery(id+"F0.wireOp",EDGE,"E164"),sQuery(id+"F0.wireOp",EDGE,"E165"),sQuery(id+"F0.wireOp",EDGE,"E166"),sQuery(id+"F0.wireOp",EDGE,"E167"),sQuery(id+"F0.wireOp",EDGE,"E168"),sQuery(id+"F7.wireOp",EDGE,"E178"),sQuery(id+"F7.wireOp",EDGE,"E180"),sQuery(id+"F7.wireOp",EDGE,"E181"),sQuery(id+"F30.wireOp",EDGE,"E278.bottom"),sQuery(id+"F30.wireOp",EDGE,"E278.top"),sQuery(id+"F30.wireOp",EDGE,"E278.left"),sQuery(id+"F30.wireOp",EDGE,"E278.right")])],"isStart":false});
            var sketch = newSketch(context, id + "F35", { "sketchPlane" : qUnion([Q0])});
            skLineSegment(sketch, "E292", {"start": v(-762, -1403.47) * mm, "end": v(-762, -2419.47) * mm});
            skLineSegment(sketch, "E293", {"start": v(-762, -2419.47) * mm, "end": v(0, -2419.47) * mm});
            skLineSegment(sketch, "E294", {"start": v(0, -2419.47) * mm, "end": v(0, -1403.47) * mm});
            skLineSegment(sketch, "E295", {"start": v(0, -1403.47) * mm, "end": v(-762, -1403.47) * mm});
            skSolve(sketch);
        }
        {
            var Q0;
            Q0 = qSketchRegion(id + "F35", true);
            extrude(context, id + "F36", {"entities" : qUnion([Q0]), "oppositeDirection" : true, "depth" : 76.2 * mm, "offsetDistance" : 25.4 * mm});
        }
        {
            var Q0;
            Q0=makeQuery(id+"F31.opExtrude","CAP_FACE",FACE,{"disambiguationData":[OSD([sQuery(id+"F0.wireOp",EDGE,"E1"),sQuery(id+"F0.wireOp",EDGE,"E2"),sQuery(id+"F0.wireOp",EDGE,"E3"),sQuery(id+"F0.wireOp",EDGE,"E4"),sQuery(id+"F0.wireOp",EDGE,"E6"),sQuery(id+"F0.wireOp",EDGE,"E7"),sQuery(id+"F0.wireOp",EDGE,"E8"),sQuery(id+"F0.wireOp",EDGE,"E9"),sQuery(id+"F0.wireOp",EDGE,"E10"),sQuery(id+"F0.wireOp",EDGE,"E11"),sQuery(id+"F0.wireOp",EDGE,"E12"),sQuery(id+"F0.wireOp",EDGE,"E13"),sQuery(id+"F0.wireOp",EDGE,"E19"),sQuery(id+"F0.wireOp",EDGE,"E20"),sQuery(id+"F0.wireOp",EDGE,"E21"),sQuery(id+"F0.wireOp",EDGE,"E22"),sQuery(id+"F0.wireOp",EDGE,"E24"),sQuery(id+"F0.wireOp",EDGE,"E25"),sQuery(id+"F0.wireOp",EDGE,"E26"),sQuery(id+"F0.wireOp",EDGE,"E27"),sQuery(id+"F0.wireOp",EDGE,"E28"),sQuery(id+"F0.wireOp",EDGE,"E29"),sQuery(id+"F0.wireOp",EDGE,"E30"),sQuery(id+"F0.wireOp",EDGE,"E31"),sQuery(id+"F0.wireOp",EDGE,"E32"),sQuery(id+"F0.wireOp",EDGE,"E34"),sQuery(id+"F0.wireOp",EDGE,"E35"),sQuery(id+"F0.wireOp",EDGE,"E36"),sQuery(id+"F0.wireOp",EDGE,"E37"),sQuery(id+"F0.wireOp",EDGE,"E38"),sQuery(id+"F0.wireOp",EDGE,"E39"),sQuery(id+"F0.wireOp",EDGE,"E40"),sQuery(id+"F0.wireOp",EDGE,"E41"),sQuery(id+"F0.wireOp",EDGE,"E42"),sQuery(id+"F0.wireOp",EDGE,"E43"),sQuery(id+"F0.wireOp",EDGE,"E44"),sQuery(id+"F0.wireOp",EDGE,"E45"),sQuery(id+"F0.wireOp",EDGE,"E46"),sQuery(id+"F0.wireOp",EDGE,"E47"),sQuery(id+"F0.wireOp",EDGE,"E48"),sQuery(id+"F0.wireOp",EDGE,"E49"),sQuery(id+"F0.wireOp",EDGE,"E50"),sQuery(id+"F0.wireOp",EDGE,"E51"),sQuery(id+"F0.wireOp",EDGE,"E52"),sQuery(id+"F0.wireOp",EDGE,"E53"),sQuery(id+"F0.wireOp",EDGE,"E54"),sQuery(id+"F0.wireOp",EDGE,"E55"),sQuery(id+"F0.wireOp",EDGE,"E56"),sQuery(id+"F0.wireOp",EDGE,"E57"),sQuery(id+"F0.wireOp",EDGE,"E58"),sQuery(id+"F0.wireOp",EDGE,"E59"),sQuery(id+"F0.wireOp",EDGE,"E60"),sQuery(id+"F0.wireOp",EDGE,"E61"),sQuery(id+"F0.wireOp",EDGE,"E62"),sQuery(id+"F0.wireOp",EDGE,"E63"),sQuery(id+"F0.wireOp",EDGE,"E64"),sQuery(id+"F0.wireOp",EDGE,"E65"),sQuery(id+"F0.wireOp",EDGE,"E66"),sQuery(id+"F0.wireOp",EDGE,"E67"),sQuery(id+"F0.wireOp",EDGE,"E68"),sQuery(id+"F0.wireOp",EDGE,"E69"),sQuery(id+"F0.wireOp",EDGE,"E70"),sQuery(id+"F0.wireOp",EDGE,"E71"),sQuery(id+"F0.wireOp",EDGE,"E72"),sQuery(id+"F0.wireOp",EDGE,"E73"),sQuery(id+"F0.wireOp",EDGE,"E74"),sQuery(id+"F0.wireOp",EDGE,"E75"),sQuery(id+"F0.wireOp",EDGE,"E76"),sQuery(id+"F0.wireOp",EDGE,"E77"),sQuery(id+"F0.wireOp",EDGE,"E78"),sQuery(id+"F0.wireOp",EDGE,"E79"),sQuery(id+"F0.wireOp",EDGE,"E80"),sQuery(id+"F0.wireOp",EDGE,"E81"),sQuery(id+"F0.wireOp",EDGE,"E82"),sQuery(id+"F0.wireOp",EDGE,"E83"),sQuery(id+"F0.wireOp",EDGE,"E84"),sQuery(id+"F0.wireOp",EDGE,"E85"),sQuery(id+"F0.wireOp",EDGE,"E86"),sQuery(id+"F0.wireOp",EDGE,"E87"),sQuery(id+"F0.wireOp",EDGE,"E88"),sQuery(id+"F0.wireOp",EDGE,"E89"),sQuery(id+"F0.wireOp",EDGE,"E90"),sQuery(id+"F0.wireOp",EDGE,"E91"),sQuery(id+"F0.wireOp",EDGE,"E94"),sQuery(id+"F0.wireOp",EDGE,"E95"),sQuery(id+"F0.wireOp",EDGE,"E98"),sQuery(id+"F0.wireOp",EDGE,"E99"),sQuery(id+"F0.wireOp",EDGE,"E100"),sQuery(id+"F0.wireOp",EDGE,"E101"),sQuery(id+"F0.wireOp",EDGE,"E102"),sQuery(id+"F0.wireOp",EDGE,"E103"),sQuery(id+"F0.wireOp",EDGE,"E104"),sQuery(id+"F0.wireOp",EDGE,"E105"),sQuery(id+"F0.wireOp",EDGE,"E106"),sQuery(id+"F0.wireOp",EDGE,"E107"),sQuery(id+"F0.wireOp",EDGE,"E108"),sQuery(id+"F0.wireOp",EDGE,"E109"),sQuery(id+"F0.wireOp",EDGE,"E110"),sQuery(id+"F0.wireOp",EDGE,"E111"),sQuery(id+"F0.wireOp",EDGE,"E112"),sQuery(id+"F0.wireOp",EDGE,"E113"),sQuery(id+"F0.wireOp",EDGE,"E114"),sQuery(id+"F0.wireOp",EDGE,"E115"),sQuery(id+"F0.wireOp",EDGE,"E116"),sQuery(id+"F0.wireOp",EDGE,"E117"),sQuery(id+"F0.wireOp",EDGE,"E118"),sQuery(id+"F0.wireOp",EDGE,"E119"),sQuery(id+"F0.wireOp",EDGE,"E120"),sQuery(id+"F0.wireOp",EDGE,"E121"),sQuery(id+"F0.wireOp",EDGE,"E122"),sQuery(id+"F0.wireOp",EDGE,"E123"),sQuery(id+"F0.wireOp",EDGE,"E124"),sQuery(id+"F0.wireOp",EDGE,"E125"),sQuery(id+"F0.wireOp",EDGE,"E126"),sQuery(id+"F0.wireOp",EDGE,"E127"),sQuery(id+"F0.wireOp",EDGE,"E128"),sQuery(id+"F0.wireOp",EDGE,"E129"),sQuery(id+"F0.wireOp",EDGE,"E130"),sQuery(id+"F0.wireOp",EDGE,"E131"),sQuery(id+"F0.wireOp",EDGE,"E132"),sQuery(id+"F0.wireOp",EDGE,"E133"),sQuery(id+"F0.wireOp",EDGE,"E137"),sQuery(id+"F0.wireOp",EDGE,"E141"),sQuery(id+"F0.wireOp",EDGE,"E142"),sQuery(id+"F0.wireOp",EDGE,"E143"),sQuery(id+"F0.wireOp",EDGE,"E146"),sQuery(id+"F0.wireOp",EDGE,"E147"),sQuery(id+"F0.wireOp",EDGE,"E148"),sQuery(id+"F0.wireOp",EDGE,"E151"),sQuery(id+"F0.wireOp",EDGE,"E152"),sQuery(id+"F0.wireOp",EDGE,"E153"),sQuery(id+"F0.wireOp",EDGE,"E154"),sQuery(id+"F0.wireOp",EDGE,"E155"),sQuery(id+"F0.wireOp",EDGE,"E156"),sQuery(id+"F0.wireOp",EDGE,"E157"),sQuery(id+"F0.wireOp",EDGE,"E158"),sQuery(id+"F0.wireOp",EDGE,"E159"),sQuery(id+"F0.wireOp",EDGE,"E160"),sQuery(id+"F0.wireOp",EDGE,"E161"),sQuery(id+"F0.wireOp",EDGE,"E162"),sQuery(id+"F0.wireOp",EDGE,"E163"),sQuery(id+"F0.wireOp",EDGE,"E164"),sQuery(id+"F0.wireOp",EDGE,"E165"),sQuery(id+"F0.wireOp",EDGE,"E166"),sQuery(id+"F0.wireOp",EDGE,"E167"),sQuery(id+"F0.wireOp",EDGE,"E168"),sQuery(id+"F7.wireOp",EDGE,"E178"),sQuery(id+"F7.wireOp",EDGE,"E180"),sQuery(id+"F7.wireOp",EDGE,"E181"),sQuery(id+"F30.wireOp",EDGE,"E278.bottom"),sQuery(id+"F30.wireOp",EDGE,"E278.top"),sQuery(id+"F30.wireOp",EDGE,"E278.left"),sQuery(id+"F30.wireOp",EDGE,"E278.right")])],"isStart":true});
            var sketch = newSketch(context, id + "F37", { "sketchPlane" : qUnion([Q0])});
            skLineSegment(sketch, "E296", {"start": v(231.53, 2589.71) * mm, "end": v(231.53, 1192.71) * mm});
            skLineSegment(sketch, "E297", {"start": v(231.53, 1192.71) * mm, "end": v(-635, 1192.71) * mm});
            skLineSegment(sketch, "E298", {"start": v(-635, 1192.71) * mm, "end": v(-762, 1192.71) * mm});
            skLineSegment(sketch, "E299", {"start": v(-762, 1192.71) * mm, "end": v(-993.52, 1192.71) * mm});
            skLineSegment(sketch, "E300", {"start": v(-993.52, 1192.71) * mm, "end": v(-993.52, 2419.47) * mm});
            skLineSegment(sketch, "E301", {"start": v(-993.52, 2419.47) * mm, "end": v(-993.52, 2630.21) * mm});
            skLineSegment(sketch, "E302", {"start": v(-993.52, 2630.21) * mm, "end": v(231.53, 2630.21) * mm});
            skLineSegment(sketch, "E303", {"start": v(231.53, 2630.21) * mm, "end": v(231.53, 2589.71) * mm});
            skLineSegment(sketch, "E304", {"start": v(-762, 2419.47) * mm, "end": v(-762, 1403.47) * mm});
            skLineSegment(sketch, "E305", {"start": v(-762, 1403.47) * mm, "end": v(0, 1403.47) * mm});
            skLineSegment(sketch, "E306", {"start": v(0, 1403.47) * mm, "end": v(0, 2419.47) * mm});
            skLineSegment(sketch, "E307", {"start": v(0, 2419.47) * mm, "end": v(-762, 2419.47) * mm});
            skSolve(sketch);
        }
        {
            var Q0;
            Q0 = qSketchRegion(id + "F37", true);
            extrude(context, id + "F38", {"entities" : qUnion([Q0]), "oppositeDirection" : true, "depth" : 50.8 * mm, "offsetDistance" : 25.4 * mm});
        }
        {
            var Q0;
            Q0=makeQuery(id+"F38.opExtrude","CAP_FACE",FACE,{"disambiguationData":[OSD([sQuery(id+"F37.wireOp",EDGE,"E296"),sQuery(id+"F37.wireOp",EDGE,"E297"),sQuery(id+"F37.wireOp",EDGE,"E298"),sQuery(id+"F37.wireOp",EDGE,"E299"),sQuery(id+"F37.wireOp",EDGE,"E300"),sQuery(id+"F37.wireOp",EDGE,"E301"),sQuery(id+"F37.wireOp",EDGE,"E302"),sQuery(id+"F37.wireOp",EDGE,"E303"),sQuery(id+"F37.wireOp",EDGE,"E304"),sQuery(id+"F37.wireOp",EDGE,"E305"),sQuery(id+"F37.wireOp",EDGE,"E306"),sQuery(id+"F37.wireOp",EDGE,"E307")])],"isStart":true});
            extrude(context, id + "F39", {"entities" : qUnion([Q0]), "depth" : 25.4 * mm, "offsetDistance" : 25.4 * mm});
        }
        {
            var Q0;
            Q0=makeQuery(id+"F31.opExtrude","SWEPT_FACE",FACE,{"disambiguationData":[OSD([sQuery(id+"F30.wireOp",EDGE,"E278.left")])]});
            extrude(context, id + "F40", {"entities" : qUnion([Q0]), "operationType" : NewBodyOperationType.ADD, "depth" : 508 * mm, "offsetDistance" : 25.4 * mm});
        }
        {
            var Q0;
            {var subQ0=sQuery(id+"F30.wireOp",EDGE,"E278.bottom");Q0=makeQuery(id+"F40.boolean.opBoolean","MERGE",FACE,{"derivedFrom":[makeQuery(id+"F31.opExtrude","SWEPT_FACE",FACE,{"disambiguationData":[OSD([subQ0])]}),makeQuery(id+"F40.opExtrude","SWEPT_FACE",FACE,{"disambiguationData":[OSD([subQ0,sQuery(id+"F30.wireOp",EDGE,"E278.left")])]})]});}
            extrude(context, id + "F41", {"entities" : qUnion([Q0]), "operationType" : NewBodyOperationType.ADD, "depth" : 254 * mm, "offsetDistance" : 25.4 * mm});
        }
        {
            var Q0;
            {var subQ0=sQuery(id+"F30.wireOp",EDGE,"E278.top");Q0=makeQuery(id+"F40.boolean.opBoolean","MERGE",FACE,{"derivedFrom":[makeQuery(id+"F31.opExtrude","SWEPT_FACE",FACE,{"disambiguationData":[OSD([subQ0])]}),makeQuery(id+"F40.opExtrude","SWEPT_FACE",FACE,{"disambiguationData":[OSD([subQ0,sQuery(id+"F30.wireOp",EDGE,"E278.left")])]})]});}
            extrude(context, id + "F42", {"entities" : qUnion([Q0]), "operationType" : NewBodyOperationType.ADD, "depth" : 254 * mm, "offsetDistance" : 25.4 * mm});
        }
        {
            var Q0;
            Q0=makeQuery(id+"F39.opExtrude","SWEPT_FACE",FACE,{"disambiguationData":[OSD([sQuery(id+"F37.wireOp",EDGE,"E297"),sQuery(id+"F37.wireOp",EDGE,"E298"),sQuery(id+"F37.wireOp",EDGE,"E299")])]});
            var sketch = newSketch(context, id + "F43", { "sketchPlane" : qUnion([Q0])});
            skLineSegment(sketch, "E308", {"start": v(-993.52, 0) * mm, "end": v(-993.52, 25.4) * mm});
            skLineSegment(sketch, "E309.0", {"start": v(-635, 254) * mm, "end": v(-635, 0) * mm});
            skLineSegment(sketch, "E310", {"start": v(-993.52, 25.4) * mm, "end": v(-635, 25.4) * mm});
            skLineSegment(sketch, "E311", {"start": v(-635, 25.4) * mm, "end": v(-635, 0) * mm});
            skLineSegment(sketch, "E312", {"start": v(-993.52, 0) * mm, "end": v(-635, 0) * mm});
            skSolve(sketch);
        }
        {
            var Q0;
            Q0=makeQuery(id+"F10.opExtrude","CAP_FACE",FACE,{"disambiguationData":[OSD([sQuery(id+"F0.wireOp",EDGE,"E20"),sQuery(id+"F0.wireOp",EDGE,"E111"),sQuery(id+"F0.wireOp",EDGE,"E112"),sQuery(id+"F0.wireOp",EDGE,"E119"),sQuery(id+"F0.wireOp",EDGE,"E127"),sQuery(id+"F0.wireOp",EDGE,"E155")])],"isStart":false});
            var sketch = newSketch(context, id + "F44", { "sketchPlane" : qUnion([Q0])});
            skLineSegment(sketch, "E313.0", {"start": v(587.13, 254) * mm, "end": v(587.13, 0) * mm});
            skLineSegment(sketch, "E314", {"start": v(587.13, 0) * mm, "end": v(587.13, 25.4) * mm});
            skLineSegment(sketch, "E315", {"start": v(587.13, 25.4) * mm, "end": v(1346, 25.4) * mm});
            skLineSegment(sketch, "E316", {"start": v(1346, 0) * mm, "end": v(587.13, 0) * mm});
            skLineSegment(sketch, "E317.0", {"start": v(1349.13, 254) * mm, "end": v(1349.13, 0) * mm});
            skLineSegment(sketch, "E318", {"start": v(1346, 0) * mm, "end": v(1349.13, 0) * mm});
            skLineSegment(sketch, "E319", {"start": v(1349.13, 0) * mm, "end": v(1349.13, 25.4) * mm});
            skLineSegment(sketch, "E320", {"start": v(1349.13, 25.4) * mm, "end": v(1346, 25.4) * mm});
            skSolve(sketch);
        }
        {
            var Q0;
            Q0 = qSketchRegion(id + "F44", true);
            extrude(context, id + "F45", {"entities" : qUnion([Q0]), "depth" : 381 * mm, "offsetDistance" : 25.4 * mm});
        }
        {
            var Q0;
            Q0=makeQuery(id+"F41.opExtrude","CAP_FACE",FACE,{"disambiguationData":[OSD([sQuery(id+"F30.wireOp",EDGE,"E278.bottom"),sQuery(id+"F30.wireOp",EDGE,"E278.left")])],"isStart":false});
            var sketch = newSketch(context, id + "F46", { "sketchPlane" : qUnion([Q0])});
            skLineSegment(sketch, "E321.0", {"start": v(-1612.75, 0) * mm, "end": v(2950.43, 0) * mm});
            skLineSegment(sketch, "E322.0", {"start": v(1349.13, 25.4) * mm, "end": v(587.13, 25.4) * mm});
            skLineSegment(sketch, "E323.0", {"start": v(1052.6, 0) * mm, "end": v(1052.6, 254) * mm});
            skLineSegment(sketch, "E324.0", {"start": v(1205, 254) * mm, "end": v(1205, 0) * mm});
            skLineSegment(sketch, "E325", {"start": v(1052.6, 0) * mm, "end": v(1052.6, -50.8) * mm});
            skLineSegment(sketch, "E326", {"start": v(1052.6, -50.8) * mm, "end": v(1205, -50.8) * mm});
            skLineSegment(sketch, "E327", {"start": v(1205, -50.8) * mm, "end": v(1205, 0) * mm});
            skLineSegment(sketch, "E328", {"start": v(1052.6, 0) * mm, "end": v(1205, 0) * mm});
            skSolve(sketch);
        }
        {
            var Q0;
            Q0=makeQuery(id+"F46.imprint","IMPRINT",FACE,{"disambiguationData":[TD([[makeQuery(id+"F46.imprint","IMPRINT",EDGE,{"derivedFrom":sQuery(id+"F46.wireOp",EDGE,"E325")}),1.0]])]});
            extrude(context, id + "F47", {"entities" : qUnion([Q0]), "operationType" : NewBodyOperationType.REMOVE, "oppositeDirection" : true, "depth" : 1016 * mm, "offsetDistance" : 25.4 * mm});
        }
        {
            var Q0;
            Q0=makeQuery(id+"F47.boolean.opBoolean","COPY",FACE,{"derivedFrom":makeQuery(id+"F47.opExtrude","CAP_FACE",FACE,{"disambiguationData":[OSD([sQuery(id+"F46.wireOp",EDGE,"E325"),sQuery(id+"F46.wireOp",EDGE,"E326"),sQuery(id+"F46.wireOp",EDGE,"E327"),sQuery(id+"F46.wireOp",EDGE,"E328")])],"isStart":false})});
            extrude(context, id + "F48", {"entities" : qUnion([Q0]), "depth" : 1016 * mm, "offsetDistance" : 25.4 * mm});
        }
        {
            var Q0;
            {var subQ0=sQuery(id+"F30.wireOp",EDGE,"E278.left");var subQ1=sQuery(id+"F30.wireOp",EDGE,"E278.top");var subQ2=sQuery(id+"F30.wireOp",EDGE,"E278.bottom");Q0=makeQuery(id+"F42.boolean.opBoolean","MERGE",FACE,{"derivedFrom":[makeQuery(id+"F41.boolean.opBoolean","MERGE",FACE,{"derivedFrom":[makeQuery(id+"F40.boolean.opBoolean","MERGE",FACE,{"derivedFrom":[makeQuery(id+"F31.opExtrude","CAP_FACE",FACE,{"disambiguationData":[OSD([sQuery(id+"F0.wireOp",EDGE,"E1"),sQuery(id+"F0.wireOp",EDGE,"E2"),sQuery(id+"F0.wireOp",EDGE,"E3"),sQuery(id+"F0.wireOp",EDGE,"E4"),sQuery(id+"F0.wireOp",EDGE,"E6"),sQuery(id+"F0.wireOp",EDGE,"E7"),sQuery(id+"F0.wireOp",EDGE,"E8"),sQuery(id+"F0.wireOp",EDGE,"E9"),sQuery(id+"F0.wireOp",EDGE,"E10"),sQuery(id+"F0.wireOp",EDGE,"E11"),sQuery(id+"F0.wireOp",EDGE,"E12"),sQuery(id+"F0.wireOp",EDGE,"E13"),sQuery(id+"F0.wireOp",EDGE,"E19"),sQuery(id+"F0.wireOp",EDGE,"E20"),sQuery(id+"F0.wireOp",EDGE,"E21"),sQuery(id+"F0.wireOp",EDGE,"E22"),sQuery(id+"F0.wireOp",EDGE,"E24"),sQuery(id+"F0.wireOp",EDGE,"E25"),sQuery(id+"F0.wireOp",EDGE,"E26"),sQuery(id+"F0.wireOp",EDGE,"E27"),sQuery(id+"F0.wireOp",EDGE,"E28"),sQuery(id+"F0.wireOp",EDGE,"E29"),sQuery(id+"F0.wireOp",EDGE,"E30"),sQuery(id+"F0.wireOp",EDGE,"E31"),sQuery(id+"F0.wireOp",EDGE,"E32"),sQuery(id+"F0.wireOp",EDGE,"E34"),sQuery(id+"F0.wireOp",EDGE,"E35"),sQuery(id+"F0.wireOp",EDGE,"E36"),sQuery(id+"F0.wireOp",EDGE,"E37"),sQuery(id+"F0.wireOp",EDGE,"E38"),sQuery(id+"F0.wireOp",EDGE,"E39"),sQuery(id+"F0.wireOp",EDGE,"E40"),sQuery(id+"F0.wireOp",EDGE,"E41"),sQuery(id+"F0.wireOp",EDGE,"E42"),sQuery(id+"F0.wireOp",EDGE,"E43"),sQuery(id+"F0.wireOp",EDGE,"E44"),sQuery(id+"F0.wireOp",EDGE,"E45"),sQuery(id+"F0.wireOp",EDGE,"E46"),sQuery(id+"F0.wireOp",EDGE,"E47"),sQuery(id+"F0.wireOp",EDGE,"E48"),sQuery(id+"F0.wireOp",EDGE,"E49"),sQuery(id+"F0.wireOp",EDGE,"E50"),sQuery(id+"F0.wireOp",EDGE,"E51"),sQuery(id+"F0.wireOp",EDGE,"E52"),sQuery(id+"F0.wireOp",EDGE,"E53"),sQuery(id+"F0.wireOp",EDGE,"E54"),sQuery(id+"F0.wireOp",EDGE,"E55"),sQuery(id+"F0.wireOp",EDGE,"E56"),sQuery(id+"F0.wireOp",EDGE,"E57"),sQuery(id+"F0.wireOp",EDGE,"E58"),sQuery(id+"F0.wireOp",EDGE,"E59"),sQuery(id+"F0.wireOp",EDGE,"E60"),sQuery(id+"F0.wireOp",EDGE,"E61"),sQuery(id+"F0.wireOp",EDGE,"E62"),sQuery(id+"F0.wireOp",EDGE,"E63"),sQuery(id+"F0.wireOp",EDGE,"E64"),sQuery(id+"F0.wireOp",EDGE,"E65"),sQuery(id+"F0.wireOp",EDGE,"E66"),sQuery(id+"F0.wireOp",EDGE,"E67"),sQuery(id+"F0.wireOp",EDGE,"E68"),sQuery(id+"F0.wireOp",EDGE,"E69"),sQuery(id+"F0.wireOp",EDGE,"E70"),sQuery(id+"F0.wireOp",EDGE,"E71"),sQuery(id+"F0.wireOp",EDGE,"E72"),sQuery(id+"F0.wireOp",EDGE,"E73"),sQuery(id+"F0.wireOp",EDGE,"E74"),sQuery(id+"F0.wireOp",EDGE,"E75"),sQuery(id+"F0.wireOp",EDGE,"E76"),sQuery(id+"F0.wireOp",EDGE,"E77"),sQuery(id+"F0.wireOp",EDGE,"E78"),sQuery(id+"F0.wireOp",EDGE,"E79"),sQuery(id+"F0.wireOp",EDGE,"E80"),sQuery(id+"F0.wireOp",EDGE,"E81"),sQuery(id+"F0.wireOp",EDGE,"E82"),sQuery(id+"F0.wireOp",EDGE,"E83"),sQuery(id+"F0.wireOp",EDGE,"E84"),sQuery(id+"F0.wireOp",EDGE,"E85"),sQuery(id+"F0.wireOp",EDGE,"E86"),sQuery(id+"F0.wireOp",EDGE,"E87"),sQuery(id+"F0.wireOp",EDGE,"E88"),sQuery(id+"F0.wireOp",EDGE,"E89"),sQuery(id+"F0.wireOp",EDGE,"E90"),sQuery(id+"F0.wireOp",EDGE,"E91"),sQuery(id+"F0.wireOp",EDGE,"E94"),sQuery(id+"F0.wireOp",EDGE,"E95"),sQuery(id+"F0.wireOp",EDGE,"E98"),sQuery(id+"F0.wireOp",EDGE,"E99"),sQuery(id+"F0.wireOp",EDGE,"E100"),sQuery(id+"F0.wireOp",EDGE,"E101"),sQuery(id+"F0.wireOp",EDGE,"E102"),sQuery(id+"F0.wireOp",EDGE,"E103"),sQuery(id+"F0.wireOp",EDGE,"E104"),sQuery(id+"F0.wireOp",EDGE,"E105"),sQuery(id+"F0.wireOp",EDGE,"E106"),sQuery(id+"F0.wireOp",EDGE,"E107"),sQuery(id+"F0.wireOp",EDGE,"E108"),sQuery(id+"F0.wireOp",EDGE,"E109"),sQuery(id+"F0.wireOp",EDGE,"E110"),sQuery(id+"F0.wireOp",EDGE,"E111"),sQuery(id+"F0.wireOp",EDGE,"E112"),sQuery(id+"F0.wireOp",EDGE,"E113"),sQuery(id+"F0.wireOp",EDGE,"E114"),sQuery(id+"F0.wireOp",EDGE,"E115"),sQuery(id+"F0.wireOp",EDGE,"E116"),sQuery(id+"F0.wireOp",EDGE,"E117"),sQuery(id+"F0.wireOp",EDGE,"E118"),sQuery(id+"F0.wireOp",EDGE,"E119"),sQuery(id+"F0.wireOp",EDGE,"E120"),sQuery(id+"F0.wireOp",EDGE,"E121"),sQuery(id+"F0.wireOp",EDGE,"E122"),sQuery(id+"F0.wireOp",EDGE,"E123"),sQuery(id+"F0.wireOp",EDGE,"E124"),sQuery(id+"F0.wireOp",EDGE,"E125"),sQuery(id+"F0.wireOp",EDGE,"E126"),sQuery(id+"F0.wireOp",EDGE,"E127"),sQuery(id+"F0.wireOp",EDGE,"E128"),sQuery(id+"F0.wireOp",EDGE,"E129"),sQuery(id+"F0.wireOp",EDGE,"E130"),sQuery(id+"F0.wireOp",EDGE,"E131"),sQuery(id+"F0.wireOp",EDGE,"E132"),sQuery(id+"F0.wireOp",EDGE,"E133"),sQuery(id+"F0.wireOp",EDGE,"E137"),sQuery(id+"F0.wireOp",EDGE,"E141"),sQuery(id+"F0.wireOp",EDGE,"E142"),sQuery(id+"F0.wireOp",EDGE,"E143"),sQuery(id+"F0.wireOp",EDGE,"E146"),sQuery(id+"F0.wireOp",EDGE,"E147"),sQuery(id+"F0.wireOp",EDGE,"E148"),sQuery(id+"F0.wireOp",EDGE,"E151"),sQuery(id+"F0.wireOp",EDGE,"E152"),sQuery(id+"F0.wireOp",EDGE,"E153"),sQuery(id+"F0.wireOp",EDGE,"E154"),sQuery(id+"F0.wireOp",EDGE,"E155"),sQuery(id+"F0.wireOp",EDGE,"E156"),sQuery(id+"F0.wireOp",EDGE,"E157"),sQuery(id+"F0.wireOp",EDGE,"E158"),sQuery(id+"F0.wireOp",EDGE,"E159"),sQuery(id+"F0.wireOp",EDGE,"E160"),sQuery(id+"F0.wireOp",EDGE,"E161"),sQuery(id+"F0.wireOp",EDGE,"E162"),sQuery(id+"F0.wireOp",EDGE,"E163"),sQuery(id+"F0.wireOp",EDGE,"E164"),sQuery(id+"F0.wireOp",EDGE,"E165"),sQuery(id+"F0.wireOp",EDGE,"E166"),sQuery(id+"F0.wireOp",EDGE,"E167"),sQuery(id+"F0.wireOp",EDGE,"E168"),sQuery(id+"F7.wireOp",EDGE,"E178"),sQuery(id+"F7.wireOp",EDGE,"E180"),sQuery(id+"F7.wireOp",EDGE,"E181"),subQ2,subQ1,subQ0,sQuery(id+"F30.wireOp",EDGE,"E278.right")])],"isStart":true}),makeQuery(id+"F40.opExtrude","SWEPT_FACE",FACE,{"disambiguationData":[OSD([subQ0]),TDD([makeQuery(id+"F31.opExtrude","CAP_EDGE",EDGE,{"disambiguationData":[OSD([subQ0])],"isStart":true})])]})]}),makeQuery(id+"F41.opExtrude","SWEPT_FACE",FACE,{"disambiguationData":[OSD([subQ2,subQ0]),TDD([makeQuery(id+"F40.boolean.opBoolean","MERGE",EDGE,{"derivedFrom":[makeQuery(id+"F31.opExtrude","CAP_EDGE",EDGE,{"disambiguationData":[OSD([subQ2])],"isStart":true}),makeQuery(id+"F40.opExtrude","SWEPT_EDGE",EDGE,{"disambiguationData":[OSD([subQ2,subQ0]),TDD([makeQuery(id+"F31.opExtrude","CAP_VERTEX",VERTEX,{"disambiguationData":[OSD([subQ2,subQ0])],"isStart":true})])]})]})])]})]}),makeQuery(id+"F42.opExtrude","SWEPT_FACE",FACE,{"disambiguationData":[OSD([subQ1,subQ0]),TDD([makeQuery(id+"F40.boolean.opBoolean","MERGE",EDGE,{"derivedFrom":[makeQuery(id+"F31.opExtrude","CAP_EDGE",EDGE,{"disambiguationData":[OSD([subQ1])],"isStart":true}),makeQuery(id+"F40.opExtrude","SWEPT_EDGE",EDGE,{"disambiguationData":[OSD([subQ1,subQ0]),TDD([makeQuery(id+"F31.opExtrude","CAP_VERTEX",VERTEX,{"disambiguationData":[OSD([subQ1,subQ0])],"isStart":true})])]})]})])]})]});}
            var sketch = newSketch(context, id + "F49", { "sketchPlane" : qUnion([Q0])});
            skLineSegment(sketch, "E329", {"start": v(1052.6, -851.15) * mm, "end": v(900.2, -851.15) * mm});
            skLineSegment(sketch, "E330", {"start": v(900.2, -851.15) * mm, "end": v(900.2, -698.75) * mm});
            skLineSegment(sketch, "E331", {"start": v(900.2, -698.75) * mm, "end": v(1052.6, -698.75) * mm});
            skLineSegment(sketch, "E332", {"start": v(1052.6, -698.75) * mm, "end": v(1052.6, -851.15) * mm});
            skLineSegment(sketch, "E333", {"start": v(1052.6, -851.15) * mm, "end": v(1205, -851.15) * mm});
            skLineSegment(sketch, "E334.MirrorCS", {"start": v(1205, -698.75) * mm, "end": v(1205, -851.15) * mm});
            skLineSegment(sketch, "E335.MirrorCS", {"start": v(1357.4, -698.75) * mm, "end": v(1205, -698.75) * mm});
            skLineSegment(sketch, "E336.MirrorCS", {"start": v(1357.4, -851.15) * mm, "end": v(1357.4, -698.75) * mm});
            skLineSegment(sketch, "E337.MirrorCS", {"start": v(1205, -851.15) * mm, "end": v(1357.4, -851.15) * mm});
            skSolve(sketch);
        }
        {
            var Q0;
            Q0 = qSketchRegion(id + "F49", true);
            extrude(context, id + "F50", {"entities" : qUnion([Q0]), "depth" : 177.8 * mm, "offsetDistance" : 25.4 * mm});
        }
        {
            var Q0;
            Q0=makeQuery(id+"F50.opExtrude","SWEPT_FACE",FACE,{"disambiguationData":[OSD([sQuery(id+"F49.wireOp",EDGE,"E336.MirrorCS")])]});
            var sketch = newSketch(context, id + "F51", { "sketchPlane" : qUnion([Q0])});
            skLineSegment(sketch, "E338", {"start": v(-851.15, 0) * mm, "end": v(-698.75, 0) * mm});
            skLineSegment(sketch, "E339", {"start": v(-774.95, 0) * mm, "end": v(-800.35, 0) * mm});
            skLineSegment(sketch, "E340", {"start": v(-800.35, 0) * mm, "end": v(-749.55, 0) * mm});
            skLineSegment(sketch, "E341", {"start": v(-749.55, 0) * mm, "end": v(-749.55, 101.6) * mm});
            skLineSegment(sketch, "E342", {"start": v(-749.55, 101.6) * mm, "end": v(-800.35, 101.6) * mm});
            skLineSegment(sketch, "E343", {"start": v(-800.35, 101.6) * mm, "end": v(-800.35, 0) * mm});
            skSolve(sketch);
        }
        {
            var Q0;
            Q0 = qSketchRegion(id + "F51", true);
            extrude(context, id + "F52", {"entities" : qUnion([Q0]), "depth" : 1524 * mm, "offsetDistance" : 25.4 * mm});
        }
        {
            var Q0;
            {var subQ0=sQuery(id+"F30.wireOp",EDGE,"E278.left");var subQ1=sQuery(id+"F30.wireOp",EDGE,"E278.top");var subQ2=sQuery(id+"F30.wireOp",EDGE,"E278.bottom");Q0=makeQuery(id+"F42.boolean.opBoolean","MERGE",FACE,{"derivedFrom":[makeQuery(id+"F41.boolean.opBoolean","MERGE",FACE,{"derivedFrom":[makeQuery(id+"F40.boolean.opBoolean","MERGE",FACE,{"derivedFrom":[makeQuery(id+"F31.opExtrude","CAP_FACE",FACE,{"disambiguationData":[OSD([sQuery(id+"F0.wireOp",EDGE,"E1"),sQuery(id+"F0.wireOp",EDGE,"E2"),sQuery(id+"F0.wireOp",EDGE,"E3"),sQuery(id+"F0.wireOp",EDGE,"E4"),sQuery(id+"F0.wireOp",EDGE,"E6"),sQuery(id+"F0.wireOp",EDGE,"E7"),sQuery(id+"F0.wireOp",EDGE,"E8"),sQuery(id+"F0.wireOp",EDGE,"E9"),sQuery(id+"F0.wireOp",EDGE,"E10"),sQuery(id+"F0.wireOp",EDGE,"E11"),sQuery(id+"F0.wireOp",EDGE,"E12"),sQuery(id+"F0.wireOp",EDGE,"E13"),sQuery(id+"F0.wireOp",EDGE,"E19"),sQuery(id+"F0.wireOp",EDGE,"E20"),sQuery(id+"F0.wireOp",EDGE,"E21"),sQuery(id+"F0.wireOp",EDGE,"E22"),sQuery(id+"F0.wireOp",EDGE,"E24"),sQuery(id+"F0.wireOp",EDGE,"E25"),sQuery(id+"F0.wireOp",EDGE,"E26"),sQuery(id+"F0.wireOp",EDGE,"E27"),sQuery(id+"F0.wireOp",EDGE,"E28"),sQuery(id+"F0.wireOp",EDGE,"E29"),sQuery(id+"F0.wireOp",EDGE,"E30"),sQuery(id+"F0.wireOp",EDGE,"E31"),sQuery(id+"F0.wireOp",EDGE,"E32"),sQuery(id+"F0.wireOp",EDGE,"E34"),sQuery(id+"F0.wireOp",EDGE,"E35"),sQuery(id+"F0.wireOp",EDGE,"E36"),sQuery(id+"F0.wireOp",EDGE,"E37"),sQuery(id+"F0.wireOp",EDGE,"E38"),sQuery(id+"F0.wireOp",EDGE,"E39"),sQuery(id+"F0.wireOp",EDGE,"E40"),sQuery(id+"F0.wireOp",EDGE,"E41"),sQuery(id+"F0.wireOp",EDGE,"E42"),sQuery(id+"F0.wireOp",EDGE,"E43"),sQuery(id+"F0.wireOp",EDGE,"E44"),sQuery(id+"F0.wireOp",EDGE,"E45"),sQuery(id+"F0.wireOp",EDGE,"E46"),sQuery(id+"F0.wireOp",EDGE,"E47"),sQuery(id+"F0.wireOp",EDGE,"E48"),sQuery(id+"F0.wireOp",EDGE,"E49"),sQuery(id+"F0.wireOp",EDGE,"E50"),sQuery(id+"F0.wireOp",EDGE,"E51"),sQuery(id+"F0.wireOp",EDGE,"E52"),sQuery(id+"F0.wireOp",EDGE,"E53"),sQuery(id+"F0.wireOp",EDGE,"E54"),sQuery(id+"F0.wireOp",EDGE,"E55"),sQuery(id+"F0.wireOp",EDGE,"E56"),sQuery(id+"F0.wireOp",EDGE,"E57"),sQuery(id+"F0.wireOp",EDGE,"E58"),sQuery(id+"F0.wireOp",EDGE,"E59"),sQuery(id+"F0.wireOp",EDGE,"E60"),sQuery(id+"F0.wireOp",EDGE,"E61"),sQuery(id+"F0.wireOp",EDGE,"E62"),sQuery(id+"F0.wireOp",EDGE,"E63"),sQuery(id+"F0.wireOp",EDGE,"E64"),sQuery(id+"F0.wireOp",EDGE,"E65"),sQuery(id+"F0.wireOp",EDGE,"E66"),sQuery(id+"F0.wireOp",EDGE,"E67"),sQuery(id+"F0.wireOp",EDGE,"E68"),sQuery(id+"F0.wireOp",EDGE,"E69"),sQuery(id+"F0.wireOp",EDGE,"E70"),sQuery(id+"F0.wireOp",EDGE,"E71"),sQuery(id+"F0.wireOp",EDGE,"E72"),sQuery(id+"F0.wireOp",EDGE,"E73"),sQuery(id+"F0.wireOp",EDGE,"E74"),sQuery(id+"F0.wireOp",EDGE,"E75"),sQuery(id+"F0.wireOp",EDGE,"E76"),sQuery(id+"F0.wireOp",EDGE,"E77"),sQuery(id+"F0.wireOp",EDGE,"E78"),sQuery(id+"F0.wireOp",EDGE,"E79"),sQuery(id+"F0.wireOp",EDGE,"E80"),sQuery(id+"F0.wireOp",EDGE,"E81"),sQuery(id+"F0.wireOp",EDGE,"E82"),sQuery(id+"F0.wireOp",EDGE,"E83"),sQuery(id+"F0.wireOp",EDGE,"E84"),sQuery(id+"F0.wireOp",EDGE,"E85"),sQuery(id+"F0.wireOp",EDGE,"E86"),sQuery(id+"F0.wireOp",EDGE,"E87"),sQuery(id+"F0.wireOp",EDGE,"E88"),sQuery(id+"F0.wireOp",EDGE,"E89"),sQuery(id+"F0.wireOp",EDGE,"E90"),sQuery(id+"F0.wireOp",EDGE,"E91"),sQuery(id+"F0.wireOp",EDGE,"E94"),sQuery(id+"F0.wireOp",EDGE,"E95"),sQuery(id+"F0.wireOp",EDGE,"E98"),sQuery(id+"F0.wireOp",EDGE,"E99"),sQuery(id+"F0.wireOp",EDGE,"E100"),sQuery(id+"F0.wireOp",EDGE,"E101"),sQuery(id+"F0.wireOp",EDGE,"E102"),sQuery(id+"F0.wireOp",EDGE,"E103"),sQuery(id+"F0.wireOp",EDGE,"E104"),sQuery(id+"F0.wireOp",EDGE,"E105"),sQuery(id+"F0.wireOp",EDGE,"E106"),sQuery(id+"F0.wireOp",EDGE,"E107"),sQuery(id+"F0.wireOp",EDGE,"E108"),sQuery(id+"F0.wireOp",EDGE,"E109"),sQuery(id+"F0.wireOp",EDGE,"E110"),sQuery(id+"F0.wireOp",EDGE,"E111"),sQuery(id+"F0.wireOp",EDGE,"E112"),sQuery(id+"F0.wireOp",EDGE,"E113"),sQuery(id+"F0.wireOp",EDGE,"E114"),sQuery(id+"F0.wireOp",EDGE,"E115"),sQuery(id+"F0.wireOp",EDGE,"E116"),sQuery(id+"F0.wireOp",EDGE,"E117"),sQuery(id+"F0.wireOp",EDGE,"E118"),sQuery(id+"F0.wireOp",EDGE,"E119"),sQuery(id+"F0.wireOp",EDGE,"E120"),sQuery(id+"F0.wireOp",EDGE,"E121"),sQuery(id+"F0.wireOp",EDGE,"E122"),sQuery(id+"F0.wireOp",EDGE,"E123"),sQuery(id+"F0.wireOp",EDGE,"E124"),sQuery(id+"F0.wireOp",EDGE,"E125"),sQuery(id+"F0.wireOp",EDGE,"E126"),sQuery(id+"F0.wireOp",EDGE,"E127"),sQuery(id+"F0.wireOp",EDGE,"E128"),sQuery(id+"F0.wireOp",EDGE,"E129"),sQuery(id+"F0.wireOp",EDGE,"E130"),sQuery(id+"F0.wireOp",EDGE,"E131"),sQuery(id+"F0.wireOp",EDGE,"E132"),sQuery(id+"F0.wireOp",EDGE,"E133"),sQuery(id+"F0.wireOp",EDGE,"E137"),sQuery(id+"F0.wireOp",EDGE,"E141"),sQuery(id+"F0.wireOp",EDGE,"E142"),sQuery(id+"F0.wireOp",EDGE,"E143"),sQuery(id+"F0.wireOp",EDGE,"E146"),sQuery(id+"F0.wireOp",EDGE,"E147"),sQuery(id+"F0.wireOp",EDGE,"E148"),sQuery(id+"F0.wireOp",EDGE,"E151"),sQuery(id+"F0.wireOp",EDGE,"E152"),sQuery(id+"F0.wireOp",EDGE,"E153"),sQuery(id+"F0.wireOp",EDGE,"E154"),sQuery(id+"F0.wireOp",EDGE,"E155"),sQuery(id+"F0.wireOp",EDGE,"E156"),sQuery(id+"F0.wireOp",EDGE,"E157"),sQuery(id+"F0.wireOp",EDGE,"E158"),sQuery(id+"F0.wireOp",EDGE,"E159"),sQuery(id+"F0.wireOp",EDGE,"E160"),sQuery(id+"F0.wireOp",EDGE,"E161"),sQuery(id+"F0.wireOp",EDGE,"E162"),sQuery(id+"F0.wireOp",EDGE,"E163"),sQuery(id+"F0.wireOp",EDGE,"E164"),sQuery(id+"F0.wireOp",EDGE,"E165"),sQuery(id+"F0.wireOp",EDGE,"E166"),sQuery(id+"F0.wireOp",EDGE,"E167"),sQuery(id+"F0.wireOp",EDGE,"E168"),sQuery(id+"F7.wireOp",EDGE,"E178"),sQuery(id+"F7.wireOp",EDGE,"E180"),sQuery(id+"F7.wireOp",EDGE,"E181"),subQ2,subQ1,subQ0,sQuery(id+"F30.wireOp",EDGE,"E278.right")])],"isStart":true}),makeQuery(id+"F40.opExtrude","SWEPT_FACE",FACE,{"disambiguationData":[OSD([subQ0]),TDD([makeQuery(id+"F31.opExtrude","CAP_EDGE",EDGE,{"disambiguationData":[OSD([subQ0])],"isStart":true})])]})]}),makeQuery(id+"F41.opExtrude","SWEPT_FACE",FACE,{"disambiguationData":[OSD([subQ2,subQ0]),TDD([makeQuery(id+"F40.boolean.opBoolean","MERGE",EDGE,{"derivedFrom":[makeQuery(id+"F31.opExtrude","CAP_EDGE",EDGE,{"disambiguationData":[OSD([subQ2])],"isStart":true}),makeQuery(id+"F40.opExtrude","SWEPT_EDGE",EDGE,{"disambiguationData":[OSD([subQ2,subQ0]),TDD([makeQuery(id+"F31.opExtrude","CAP_VERTEX",VERTEX,{"disambiguationData":[OSD([subQ2,subQ0])],"isStart":true})])]})]})])]})]}),makeQuery(id+"F42.opExtrude","SWEPT_FACE",FACE,{"disambiguationData":[OSD([subQ1,subQ0]),TDD([makeQuery(id+"F40.boolean.opBoolean","MERGE",EDGE,{"derivedFrom":[makeQuery(id+"F31.opExtrude","CAP_EDGE",EDGE,{"disambiguationData":[OSD([subQ1])],"isStart":true}),makeQuery(id+"F40.opExtrude","SWEPT_EDGE",EDGE,{"disambiguationData":[OSD([subQ1,subQ0]),TDD([makeQuery(id+"F31.opExtrude","CAP_VERTEX",VERTEX,{"disambiguationData":[OSD([subQ1,subQ0])],"isStart":true})])]})]})])]})]});}
            var sketch = newSketch(context, id + "F53", { "sketchPlane" : qUnion([Q0])});
            skLineSegment(sketch, "E344", {"start": v(2950.43, -851.15) * mm, "end": v(2798.03, -851.15) * mm});
            skLineSegment(sketch, "E345", {"start": v(2798.03, -851.15) * mm, "end": v(2798.03, -698.75) * mm});
            skLineSegment(sketch, "E346", {"start": v(2798.03, -698.75) * mm, "end": v(2950.43, -698.75) * mm});
            skLineSegment(sketch, "E347", {"start": v(2950.43, -698.75) * mm, "end": v(2950.43, -851.15) * mm});
            skSolve(sketch);
        }
        {
            var Q0;
            Q0 = qSketchRegion(id + "F53", true);
            extrude(context, id + "F54", {"entities" : qUnion([Q0]), "depth" : 177.8 * mm, "offsetDistance" : 25.4 * mm});
        }
        {
            var Q0;
            {var subQ0=sQuery(id+"F30.wireOp",EDGE,"E278.left");var subQ1=sQuery(id+"F30.wireOp",EDGE,"E278.top");var subQ2=sQuery(id+"F30.wireOp",EDGE,"E278.bottom");Q0=makeQuery(id+"F42.boolean.opBoolean","MERGE",FACE,{"derivedFrom":[makeQuery(id+"F41.boolean.opBoolean","MERGE",FACE,{"derivedFrom":[makeQuery(id+"F40.boolean.opBoolean","MERGE",FACE,{"derivedFrom":[makeQuery(id+"F31.opExtrude","CAP_FACE",FACE,{"disambiguationData":[OSD([sQuery(id+"F0.wireOp",EDGE,"E1"),sQuery(id+"F0.wireOp",EDGE,"E2"),sQuery(id+"F0.wireOp",EDGE,"E3"),sQuery(id+"F0.wireOp",EDGE,"E4"),sQuery(id+"F0.wireOp",EDGE,"E6"),sQuery(id+"F0.wireOp",EDGE,"E7"),sQuery(id+"F0.wireOp",EDGE,"E8"),sQuery(id+"F0.wireOp",EDGE,"E9"),sQuery(id+"F0.wireOp",EDGE,"E10"),sQuery(id+"F0.wireOp",EDGE,"E11"),sQuery(id+"F0.wireOp",EDGE,"E12"),sQuery(id+"F0.wireOp",EDGE,"E13"),sQuery(id+"F0.wireOp",EDGE,"E19"),sQuery(id+"F0.wireOp",EDGE,"E20"),sQuery(id+"F0.wireOp",EDGE,"E21"),sQuery(id+"F0.wireOp",EDGE,"E22"),sQuery(id+"F0.wireOp",EDGE,"E24"),sQuery(id+"F0.wireOp",EDGE,"E25"),sQuery(id+"F0.wireOp",EDGE,"E26"),sQuery(id+"F0.wireOp",EDGE,"E27"),sQuery(id+"F0.wireOp",EDGE,"E28"),sQuery(id+"F0.wireOp",EDGE,"E29"),sQuery(id+"F0.wireOp",EDGE,"E30"),sQuery(id+"F0.wireOp",EDGE,"E31"),sQuery(id+"F0.wireOp",EDGE,"E32"),sQuery(id+"F0.wireOp",EDGE,"E34"),sQuery(id+"F0.wireOp",EDGE,"E35"),sQuery(id+"F0.wireOp",EDGE,"E36"),sQuery(id+"F0.wireOp",EDGE,"E37"),sQuery(id+"F0.wireOp",EDGE,"E38"),sQuery(id+"F0.wireOp",EDGE,"E39"),sQuery(id+"F0.wireOp",EDGE,"E40"),sQuery(id+"F0.wireOp",EDGE,"E41"),sQuery(id+"F0.wireOp",EDGE,"E42"),sQuery(id+"F0.wireOp",EDGE,"E43"),sQuery(id+"F0.wireOp",EDGE,"E44"),sQuery(id+"F0.wireOp",EDGE,"E45"),sQuery(id+"F0.wireOp",EDGE,"E46"),sQuery(id+"F0.wireOp",EDGE,"E47"),sQuery(id+"F0.wireOp",EDGE,"E48"),sQuery(id+"F0.wireOp",EDGE,"E49"),sQuery(id+"F0.wireOp",EDGE,"E50"),sQuery(id+"F0.wireOp",EDGE,"E51"),sQuery(id+"F0.wireOp",EDGE,"E52"),sQuery(id+"F0.wireOp",EDGE,"E53"),sQuery(id+"F0.wireOp",EDGE,"E54"),sQuery(id+"F0.wireOp",EDGE,"E55"),sQuery(id+"F0.wireOp",EDGE,"E56"),sQuery(id+"F0.wireOp",EDGE,"E57"),sQuery(id+"F0.wireOp",EDGE,"E58"),sQuery(id+"F0.wireOp",EDGE,"E59"),sQuery(id+"F0.wireOp",EDGE,"E60"),sQuery(id+"F0.wireOp",EDGE,"E61"),sQuery(id+"F0.wireOp",EDGE,"E62"),sQuery(id+"F0.wireOp",EDGE,"E63"),sQuery(id+"F0.wireOp",EDGE,"E64"),sQuery(id+"F0.wireOp",EDGE,"E65"),sQuery(id+"F0.wireOp",EDGE,"E66"),sQuery(id+"F0.wireOp",EDGE,"E67"),sQuery(id+"F0.wireOp",EDGE,"E68"),sQuery(id+"F0.wireOp",EDGE,"E69"),sQuery(id+"F0.wireOp",EDGE,"E70"),sQuery(id+"F0.wireOp",EDGE,"E71"),sQuery(id+"F0.wireOp",EDGE,"E72"),sQuery(id+"F0.wireOp",EDGE,"E73"),sQuery(id+"F0.wireOp",EDGE,"E74"),sQuery(id+"F0.wireOp",EDGE,"E75"),sQuery(id+"F0.wireOp",EDGE,"E76"),sQuery(id+"F0.wireOp",EDGE,"E77"),sQuery(id+"F0.wireOp",EDGE,"E78"),sQuery(id+"F0.wireOp",EDGE,"E79"),sQuery(id+"F0.wireOp",EDGE,"E80"),sQuery(id+"F0.wireOp",EDGE,"E81"),sQuery(id+"F0.wireOp",EDGE,"E82"),sQuery(id+"F0.wireOp",EDGE,"E83"),sQuery(id+"F0.wireOp",EDGE,"E84"),sQuery(id+"F0.wireOp",EDGE,"E85"),sQuery(id+"F0.wireOp",EDGE,"E86"),sQuery(id+"F0.wireOp",EDGE,"E87"),sQuery(id+"F0.wireOp",EDGE,"E88"),sQuery(id+"F0.wireOp",EDGE,"E89"),sQuery(id+"F0.wireOp",EDGE,"E90"),sQuery(id+"F0.wireOp",EDGE,"E91"),sQuery(id+"F0.wireOp",EDGE,"E94"),sQuery(id+"F0.wireOp",EDGE,"E95"),sQuery(id+"F0.wireOp",EDGE,"E98"),sQuery(id+"F0.wireOp",EDGE,"E99"),sQuery(id+"F0.wireOp",EDGE,"E100"),sQuery(id+"F0.wireOp",EDGE,"E101"),sQuery(id+"F0.wireOp",EDGE,"E102"),sQuery(id+"F0.wireOp",EDGE,"E103"),sQuery(id+"F0.wireOp",EDGE,"E104"),sQuery(id+"F0.wireOp",EDGE,"E105"),sQuery(id+"F0.wireOp",EDGE,"E106"),sQuery(id+"F0.wireOp",EDGE,"E107"),sQuery(id+"F0.wireOp",EDGE,"E108"),sQuery(id+"F0.wireOp",EDGE,"E109"),sQuery(id+"F0.wireOp",EDGE,"E110"),sQuery(id+"F0.wireOp",EDGE,"E111"),sQuery(id+"F0.wireOp",EDGE,"E112"),sQuery(id+"F0.wireOp",EDGE,"E113"),sQuery(id+"F0.wireOp",EDGE,"E114"),sQuery(id+"F0.wireOp",EDGE,"E115"),sQuery(id+"F0.wireOp",EDGE,"E116"),sQuery(id+"F0.wireOp",EDGE,"E117"),sQuery(id+"F0.wireOp",EDGE,"E118"),sQuery(id+"F0.wireOp",EDGE,"E119"),sQuery(id+"F0.wireOp",EDGE,"E120"),sQuery(id+"F0.wireOp",EDGE,"E121"),sQuery(id+"F0.wireOp",EDGE,"E122"),sQuery(id+"F0.wireOp",EDGE,"E123"),sQuery(id+"F0.wireOp",EDGE,"E124"),sQuery(id+"F0.wireOp",EDGE,"E125"),sQuery(id+"F0.wireOp",EDGE,"E126"),sQuery(id+"F0.wireOp",EDGE,"E127"),sQuery(id+"F0.wireOp",EDGE,"E128"),sQuery(id+"F0.wireOp",EDGE,"E129"),sQuery(id+"F0.wireOp",EDGE,"E130"),sQuery(id+"F0.wireOp",EDGE,"E131"),sQuery(id+"F0.wireOp",EDGE,"E132"),sQuery(id+"F0.wireOp",EDGE,"E133"),sQuery(id+"F0.wireOp",EDGE,"E137"),sQuery(id+"F0.wireOp",EDGE,"E141"),sQuery(id+"F0.wireOp",EDGE,"E142"),sQuery(id+"F0.wireOp",EDGE,"E143"),sQuery(id+"F0.wireOp",EDGE,"E146"),sQuery(id+"F0.wireOp",EDGE,"E147"),sQuery(id+"F0.wireOp",EDGE,"E148"),sQuery(id+"F0.wireOp",EDGE,"E151"),sQuery(id+"F0.wireOp",EDGE,"E152"),sQuery(id+"F0.wireOp",EDGE,"E153"),sQuery(id+"F0.wireOp",EDGE,"E154"),sQuery(id+"F0.wireOp",EDGE,"E155"),sQuery(id+"F0.wireOp",EDGE,"E156"),sQuery(id+"F0.wireOp",EDGE,"E157"),sQuery(id+"F0.wireOp",EDGE,"E158"),sQuery(id+"F0.wireOp",EDGE,"E159"),sQuery(id+"F0.wireOp",EDGE,"E160"),sQuery(id+"F0.wireOp",EDGE,"E161"),sQuery(id+"F0.wireOp",EDGE,"E162"),sQuery(id+"F0.wireOp",EDGE,"E163"),sQuery(id+"F0.wireOp",EDGE,"E164"),sQuery(id+"F0.wireOp",EDGE,"E165"),sQuery(id+"F0.wireOp",EDGE,"E166"),sQuery(id+"F0.wireOp",EDGE,"E167"),sQuery(id+"F0.wireOp",EDGE,"E168"),sQuery(id+"F7.wireOp",EDGE,"E178"),sQuery(id+"F7.wireOp",EDGE,"E180"),sQuery(id+"F7.wireOp",EDGE,"E181"),subQ2,subQ1,subQ0,sQuery(id+"F30.wireOp",EDGE,"E278.right")])],"isStart":true}),makeQuery(id+"F40.opExtrude","SWEPT_FACE",FACE,{"disambiguationData":[OSD([subQ0]),TDD([makeQuery(id+"F31.opExtrude","CAP_EDGE",EDGE,{"disambiguationData":[OSD([subQ0])],"isStart":true})])]})]}),makeQuery(id+"F41.opExtrude","SWEPT_FACE",FACE,{"disambiguationData":[OSD([subQ2,subQ0]),TDD([makeQuery(id+"F40.boolean.opBoolean","MERGE",EDGE,{"derivedFrom":[makeQuery(id+"F31.opExtrude","CAP_EDGE",EDGE,{"disambiguationData":[OSD([subQ2])],"isStart":true}),makeQuery(id+"F40.opExtrude","SWEPT_EDGE",EDGE,{"disambiguationData":[OSD([subQ2,subQ0]),TDD([makeQuery(id+"F31.opExtrude","CAP_VERTEX",VERTEX,{"disambiguationData":[OSD([subQ2,subQ0])],"isStart":true})])]})]})])]})]}),makeQuery(id+"F42.opExtrude","SWEPT_FACE",FACE,{"disambiguationData":[OSD([subQ1,subQ0]),TDD([makeQuery(id+"F40.boolean.opBoolean","MERGE",EDGE,{"derivedFrom":[makeQuery(id+"F31.opExtrude","CAP_EDGE",EDGE,{"disambiguationData":[OSD([subQ1])],"isStart":true}),makeQuery(id+"F40.opExtrude","SWEPT_EDGE",EDGE,{"disambiguationData":[OSD([subQ1,subQ0]),TDD([makeQuery(id+"F31.opExtrude","CAP_VERTEX",VERTEX,{"disambiguationData":[OSD([subQ1,subQ0])],"isStart":true})])]})]})])]})]});}
            var sketch = newSketch(context, id + "F55", { "sketchPlane" : qUnion([Q0])});
            skLineSegment(sketch, "E348", {"start": v(2950.43, 3391.36) * mm, "end": v(2798.03, 3391.36) * mm});
            skLineSegment(sketch, "E349", {"start": v(2798.03, 3391.36) * mm, "end": v(2798.03, 3238.96) * mm});
            skLineSegment(sketch, "E350", {"start": v(2798.03, 3238.96) * mm, "end": v(2950.43, 3238.96) * mm});
            skLineSegment(sketch, "E351", {"start": v(2950.43, 3238.96) * mm, "end": v(2950.43, 3391.36) * mm});
            skLineSegment(sketch, "E352", {"start": v(-1612.75, 3391.36) * mm, "end": v(-1612.75, 3238.96) * mm});
            skLineSegment(sketch, "E353", {"start": v(-1612.75, 3238.96) * mm, "end": v(-1460.35, 3238.96) * mm});
            skLineSegment(sketch, "E354", {"start": v(-1460.35, 3238.96) * mm, "end": v(-1460.35, 3391.36) * mm});
            skLineSegment(sketch, "E355", {"start": v(-1460.35, 3391.36) * mm, "end": v(-1612.75, 3391.36) * mm});
            skLineSegment(sketch, "E356", {"start": v(-1612.75, -851.15) * mm, "end": v(-1612.75, -698.75) * mm});
            skLineSegment(sketch, "E357", {"start": v(-1612.75, -698.75) * mm, "end": v(-1460.35, -698.75) * mm});
            skLineSegment(sketch, "E358", {"start": v(-1460.35, -698.75) * mm, "end": v(-1460.35, -851.15) * mm});
            skLineSegment(sketch, "E359", {"start": v(-1460.35, -851.15) * mm, "end": v(-1612.75, -851.15) * mm});
            skSolve(sketch);
        }
        {
            var Q0;
            Q0 = qSketchRegion(id + "F55", true);
            extrude(context, id + "F56", {"entities" : qUnion([Q0]), "depth" : 177.8 * mm, "offsetDistance" : 25.4 * mm});
        }
        {
            var Q0;
            Q0=makeQuery(id+"F56.opExtrude","SWEPT_FACE",FACE,{"disambiguationData":[OSD([sQuery(id+"F55.wireOp",EDGE,"E350")])]});
            var sketch = newSketch(context, id + "F57", { "sketchPlane" : qUnion([Q0])});
            skLineSegment(sketch, "E360", {"start": v(2798.03, 0) * mm, "end": v(2950.43, 0) * mm});
            skLineSegment(sketch, "E361", {"start": v(2950.43, 0) * mm, "end": v(2874.23, 0) * mm});
            skLineSegment(sketch, "E362", {"start": v(2874.23, 0) * mm, "end": v(2848.83, 0) * mm});
            skLineSegment(sketch, "E363", {"start": v(2848.83, 0) * mm, "end": v(2899.63, 0) * mm});
            skLineSegment(sketch, "E364", {"start": v(2899.63, 0) * mm, "end": v(2899.63, 101.6) * mm});
            skLineSegment(sketch, "E365", {"start": v(2899.63, 101.6) * mm, "end": v(2848.83, 101.6) * mm});
            skLineSegment(sketch, "E366", {"start": v(2848.83, 101.6) * mm, "end": v(2848.83, 0) * mm});
            skSolve(sketch);
        }
        {
            var Q0;
            Q0 = qSketchRegion(id + "F57", true);
            extrude(context, id + "F58", {"entities" : qUnion([Q0]), "depth" : 3937 * mm, "offsetDistance" : 25.4 * mm});
        }
        {
            var Q0;
            Q0=makeQuery(id+"F56.opExtrude","SWEPT_FACE",FACE,{"disambiguationData":[OSD([sQuery(id+"F55.wireOp",EDGE,"E354")])]});
            var sketch = newSketch(context, id + "F59", { "sketchPlane" : qUnion([Q0])});
            skLineSegment(sketch, "E367", {"start": v(3315.16, 0) * mm, "end": v(3289.76, 0) * mm});
            skLineSegment(sketch, "E368", {"start": v(3289.76, 0) * mm, "end": v(3340.56, 0) * mm});
            skLineSegment(sketch, "E369", {"start": v(3340.56, 0) * mm, "end": v(3340.56, 101.6) * mm});
            skLineSegment(sketch, "E370", {"start": v(3340.56, 101.6) * mm, "end": v(3289.76, 101.6) * mm});
            skLineSegment(sketch, "E371", {"start": v(3289.76, 101.6) * mm, "end": v(3289.76, 0) * mm});
            skSolve(sketch);
        }
        {
            var Q0;
            Q0 = qSketchRegion(id + "F59", true);
            extrude(context, id + "F60", {"entities" : qUnion([Q0]), "depth" : 4318 * mm, "offsetDistance" : 25.4 * mm});
        }
        {
            var Q0;
            Q0=makeQuery(id+"F56.opExtrude","SWEPT_FACE",FACE,{"disambiguationData":[OSD([sQuery(id+"F55.wireOp",EDGE,"E353")])]});
            var sketch = newSketch(context, id + "F61", { "sketchPlane" : qUnion([Q0])});
            skLineSegment(sketch, "E372", {"start": v(-1536.55, 0) * mm, "end": v(-1561.95, 0) * mm});
            skLineSegment(sketch, "E373", {"start": v(-1561.95, 0) * mm, "end": v(-1511.15, 0) * mm});
            skLineSegment(sketch, "E374", {"start": v(-1511.15, 0) * mm, "end": v(-1511.15, 101.6) * mm});
            skLineSegment(sketch, "E375", {"start": v(-1511.15, 101.6) * mm, "end": v(-1561.95, 101.6) * mm});
            skLineSegment(sketch, "E376", {"start": v(-1561.95, 101.6) * mm, "end": v(-1561.95, 0) * mm});
            skSolve(sketch);
        }
        {
            var Q0;
            Q0 = qSketchRegion(id + "F61", true);
            extrude(context, id + "F62", {"entities" : qUnion([Q0]), "depth" : 4064 * mm, "offsetDistance" : 25.4 * mm});
        }
        {
            var Q0;
            Q0=makeQuery(id+"F56.opExtrude","SWEPT_FACE",FACE,{"disambiguationData":[OSD([sQuery(id+"F55.wireOp",EDGE,"E358")])]});
            var sketch = newSketch(context, id + "F63", { "sketchPlane" : qUnion([Q0])});
            skLineSegment(sketch, "E377", {"start": v(-774.95, 0) * mm, "end": v(-800.35, 0) * mm});
            skLineSegment(sketch, "E378", {"start": v(-800.35, 0) * mm, "end": v(-749.55, 0) * mm});
            skLineSegment(sketch, "E379", {"start": v(-749.55, 0) * mm, "end": v(-749.55, 101.6) * mm});
            skLineSegment(sketch, "E380", {"start": v(-749.55, 101.6) * mm, "end": v(-800.35, 101.6) * mm});
            skLineSegment(sketch, "E381", {"start": v(-800.35, 101.6) * mm, "end": v(-800.35, 0) * mm});
            skSolve(sketch);
        }
        {
            var Q0;
            Q0=makeQuery(id+"F1.opExtrude","SWEPT_FACE",FACE,{"disambiguationData":[OSD([sQuery(id+"F0.wireOp",EDGE,"E7"),sQuery(id+"F0.wireOp",EDGE,"E94")])]});
            var sketch = newSketch(context, id + "F64", { "sketchPlane" : qUnion([Q0])});
            skLineSegment(sketch, "E382", {"start": v(-23.93, 254) * mm, "end": v(-23.93, 0) * mm});
            skLineSegment(sketch, "E383", {"start": v(-23.93, 0) * mm, "end": v(-277.93, 0) * mm});
            skLineSegment(sketch, "E384", {"start": v(-277.93, 0) * mm, "end": v(230.07, 0) * mm});
            skLineSegment(sketch, "E385.0.0", {"start": v(1052.6, -50.8) * mm, "end": v(1052.6, 0) * mm});
            skLineSegment(sketch, "E385.0.2", {"start": v(-1612.75, 0) * mm, "end": v(-1612.75, -50.8) * mm});
            skLineSegment(sketch, "E386", {"start": v(-277.93, 0) * mm, "end": v(-277.93, -50.8) * mm});
            skLineSegment(sketch, "E387", {"start": v(-277.93, -50.8) * mm, "end": v(230.07, -50.8) * mm});
            skLineSegment(sketch, "E388", {"start": v(230.07, -50.8) * mm, "end": v(230.07, 0) * mm});
            skSolve(sketch);
        }
        {
            var Q0;
            Q0 = qSketchRegion(id + "F64", true);
            extrude(context, id + "F65", {"entities" : qUnion([Q0]), "operationType" : NewBodyOperationType.ADD, "depth" : 1905 * mm, "offsetDistance" : 25.4 * mm});
        }
        {
            var Q0;
            Q0=makeQuery(id+"F65.opExtrude","CAP_FACE",FACE,{"disambiguationData":[OSD([sQuery(id+"F64.wireOp",EDGE,"E384"),sQuery(id+"F64.wireOp",EDGE,"E386"),sQuery(id+"F64.wireOp",EDGE,"E387"),sQuery(id+"F64.wireOp",EDGE,"E388")])],"isStart":false});
            extrude(context, id + "F66", {"entities" : qUnion([Q0]), "operationType" : NewBodyOperationType.REMOVE, "oppositeDirection" : true, "depth" : 1905 * mm, "offsetDistance" : 25.4 * mm});
        }
        {
            var Q0;
            {var subQ0=sQuery(id+"F64.wireOp",EDGE,"E386");Q0=makeQuery(id+"F64.imprint","IMPRINT",FACE,{"disambiguationData":[TD([[makeQuery(id+"F64.imprint","IMPRINT",EDGE,{"derivedFrom":subQ0}),1.0]])]});}
            extrude(context, id + "F67", {"entities" : qUnion([Q0]), "depth" : 799.47 * mm, "offsetDistance" : 25.4 * mm});
        }
        {
            var Q0;
            Q0=makeQuery(id+"F1.opExtrude","SWEPT_FACE",FACE,{"disambiguationData":[OSD([sQuery(id+"F0.wireOp",EDGE,"E7"),sQuery(id+"F0.wireOp",EDGE,"E94")])]});
            var sketch = newSketch(context, id + "F68", { "sketchPlane" : qUnion([Q0])});
            skLineSegment(sketch, "E389.0", {"start": v(230.07, 0) * mm, "end": v(-277.93, 0) * mm});
            skLineSegment(sketch, "E390", {"start": v(-277.93, 0) * mm, "end": v(-277.93, 152.4) * mm});
            skLineSegment(sketch, "E391", {"start": v(-277.93, 152.4) * mm, "end": v(230.07, 152.4) * mm});
            skLineSegment(sketch, "E392", {"start": v(230.07, 152.4) * mm, "end": v(230.07, 0) * mm});
            skSolve(sketch);
        }
        {
            var Q0;
            Q0 = qSketchRegion(id + "F68", true);
            extrude(context, id + "F69", {"entities" : qUnion([Q0]), "operationType" : NewBodyOperationType.REMOVE, "oppositeDirection" : true, "depth" : 76.2 * mm, "offsetDistance" : 25.4 * mm});
        }
        {
            var Q0;
            {var subQ0=sQuery(id+"F30.wireOp",EDGE,"E278.left");var subQ1=sQuery(id+"F30.wireOp",EDGE,"E278.top");var subQ2=sQuery(id+"F30.wireOp",EDGE,"E278.bottom");Q0=makeQuery(id+"F65.boolean.opBoolean","MERGE",FACE,{"derivedFrom":[makeQuery(id+"F42.boolean.opBoolean","MERGE",FACE,{"derivedFrom":[makeQuery(id+"F41.boolean.opBoolean","MERGE",FACE,{"derivedFrom":[makeQuery(id+"F40.boolean.opBoolean","MERGE",FACE,{"derivedFrom":[makeQuery(id+"F31.opExtrude","CAP_FACE",FACE,{"disambiguationData":[OSD([sQuery(id+"F0.wireOp",EDGE,"E1"),sQuery(id+"F0.wireOp",EDGE,"E2"),sQuery(id+"F0.wireOp",EDGE,"E3"),sQuery(id+"F0.wireOp",EDGE,"E4"),sQuery(id+"F0.wireOp",EDGE,"E6"),sQuery(id+"F0.wireOp",EDGE,"E7"),sQuery(id+"F0.wireOp",EDGE,"E8"),sQuery(id+"F0.wireOp",EDGE,"E9"),sQuery(id+"F0.wireOp",EDGE,"E10"),sQuery(id+"F0.wireOp",EDGE,"E11"),sQuery(id+"F0.wireOp",EDGE,"E12"),sQuery(id+"F0.wireOp",EDGE,"E13"),sQuery(id+"F0.wireOp",EDGE,"E19"),sQuery(id+"F0.wireOp",EDGE,"E20"),sQuery(id+"F0.wireOp",EDGE,"E21"),sQuery(id+"F0.wireOp",EDGE,"E22"),sQuery(id+"F0.wireOp",EDGE,"E24"),sQuery(id+"F0.wireOp",EDGE,"E25"),sQuery(id+"F0.wireOp",EDGE,"E26"),sQuery(id+"F0.wireOp",EDGE,"E27"),sQuery(id+"F0.wireOp",EDGE,"E28"),sQuery(id+"F0.wireOp",EDGE,"E29"),sQuery(id+"F0.wireOp",EDGE,"E30"),sQuery(id+"F0.wireOp",EDGE,"E31"),sQuery(id+"F0.wireOp",EDGE,"E32"),sQuery(id+"F0.wireOp",EDGE,"E34"),sQuery(id+"F0.wireOp",EDGE,"E35"),sQuery(id+"F0.wireOp",EDGE,"E36"),sQuery(id+"F0.wireOp",EDGE,"E37"),sQuery(id+"F0.wireOp",EDGE,"E38"),sQuery(id+"F0.wireOp",EDGE,"E39"),sQuery(id+"F0.wireOp",EDGE,"E40"),sQuery(id+"F0.wireOp",EDGE,"E41"),sQuery(id+"F0.wireOp",EDGE,"E42"),sQuery(id+"F0.wireOp",EDGE,"E43"),sQuery(id+"F0.wireOp",EDGE,"E44"),sQuery(id+"F0.wireOp",EDGE,"E45"),sQuery(id+"F0.wireOp",EDGE,"E46"),sQuery(id+"F0.wireOp",EDGE,"E47"),sQuery(id+"F0.wireOp",EDGE,"E48"),sQuery(id+"F0.wireOp",EDGE,"E49"),sQuery(id+"F0.wireOp",EDGE,"E50"),sQuery(id+"F0.wireOp",EDGE,"E51"),sQuery(id+"F0.wireOp",EDGE,"E52"),sQuery(id+"F0.wireOp",EDGE,"E53"),sQuery(id+"F0.wireOp",EDGE,"E54"),sQuery(id+"F0.wireOp",EDGE,"E55"),sQuery(id+"F0.wireOp",EDGE,"E56"),sQuery(id+"F0.wireOp",EDGE,"E57"),sQuery(id+"F0.wireOp",EDGE,"E58"),sQuery(id+"F0.wireOp",EDGE,"E59"),sQuery(id+"F0.wireOp",EDGE,"E60"),sQuery(id+"F0.wireOp",EDGE,"E61"),sQuery(id+"F0.wireOp",EDGE,"E62"),sQuery(id+"F0.wireOp",EDGE,"E63"),sQuery(id+"F0.wireOp",EDGE,"E64"),sQuery(id+"F0.wireOp",EDGE,"E65"),sQuery(id+"F0.wireOp",EDGE,"E66"),sQuery(id+"F0.wireOp",EDGE,"E67"),sQuery(id+"F0.wireOp",EDGE,"E68"),sQuery(id+"F0.wireOp",EDGE,"E69"),sQuery(id+"F0.wireOp",EDGE,"E70"),sQuery(id+"F0.wireOp",EDGE,"E71"),sQuery(id+"F0.wireOp",EDGE,"E72"),sQuery(id+"F0.wireOp",EDGE,"E73"),sQuery(id+"F0.wireOp",EDGE,"E74"),sQuery(id+"F0.wireOp",EDGE,"E75"),sQuery(id+"F0.wireOp",EDGE,"E76"),sQuery(id+"F0.wireOp",EDGE,"E77"),sQuery(id+"F0.wireOp",EDGE,"E78"),sQuery(id+"F0.wireOp",EDGE,"E79"),sQuery(id+"F0.wireOp",EDGE,"E80"),sQuery(id+"F0.wireOp",EDGE,"E81"),sQuery(id+"F0.wireOp",EDGE,"E82"),sQuery(id+"F0.wireOp",EDGE,"E83"),sQuery(id+"F0.wireOp",EDGE,"E84"),sQuery(id+"F0.wireOp",EDGE,"E85"),sQuery(id+"F0.wireOp",EDGE,"E86"),sQuery(id+"F0.wireOp",EDGE,"E87"),sQuery(id+"F0.wireOp",EDGE,"E88"),sQuery(id+"F0.wireOp",EDGE,"E89"),sQuery(id+"F0.wireOp",EDGE,"E90"),sQuery(id+"F0.wireOp",EDGE,"E91"),sQuery(id+"F0.wireOp",EDGE,"E94"),sQuery(id+"F0.wireOp",EDGE,"E95"),sQuery(id+"F0.wireOp",EDGE,"E98"),sQuery(id+"F0.wireOp",EDGE,"E99"),sQuery(id+"F0.wireOp",EDGE,"E100"),sQuery(id+"F0.wireOp",EDGE,"E101"),sQuery(id+"F0.wireOp",EDGE,"E102"),sQuery(id+"F0.wireOp",EDGE,"E103"),sQuery(id+"F0.wireOp",EDGE,"E104"),sQuery(id+"F0.wireOp",EDGE,"E105"),sQuery(id+"F0.wireOp",EDGE,"E106"),sQuery(id+"F0.wireOp",EDGE,"E107"),sQuery(id+"F0.wireOp",EDGE,"E108"),sQuery(id+"F0.wireOp",EDGE,"E109"),sQuery(id+"F0.wireOp",EDGE,"E110"),sQuery(id+"F0.wireOp",EDGE,"E111"),sQuery(id+"F0.wireOp",EDGE,"E112"),sQuery(id+"F0.wireOp",EDGE,"E113"),sQuery(id+"F0.wireOp",EDGE,"E114"),sQuery(id+"F0.wireOp",EDGE,"E115"),sQuery(id+"F0.wireOp",EDGE,"E116"),sQuery(id+"F0.wireOp",EDGE,"E117"),sQuery(id+"F0.wireOp",EDGE,"E118"),sQuery(id+"F0.wireOp",EDGE,"E119"),sQuery(id+"F0.wireOp",EDGE,"E120"),sQuery(id+"F0.wireOp",EDGE,"E121"),sQuery(id+"F0.wireOp",EDGE,"E122"),sQuery(id+"F0.wireOp",EDGE,"E123"),sQuery(id+"F0.wireOp",EDGE,"E124"),sQuery(id+"F0.wireOp",EDGE,"E125"),sQuery(id+"F0.wireOp",EDGE,"E126"),sQuery(id+"F0.wireOp",EDGE,"E127"),sQuery(id+"F0.wireOp",EDGE,"E128"),sQuery(id+"F0.wireOp",EDGE,"E129"),sQuery(id+"F0.wireOp",EDGE,"E130"),sQuery(id+"F0.wireOp",EDGE,"E131"),sQuery(id+"F0.wireOp",EDGE,"E132"),sQuery(id+"F0.wireOp",EDGE,"E133"),sQuery(id+"F0.wireOp",EDGE,"E137"),sQuery(id+"F0.wireOp",EDGE,"E141"),sQuery(id+"F0.wireOp",EDGE,"E142"),sQuery(id+"F0.wireOp",EDGE,"E143"),sQuery(id+"F0.wireOp",EDGE,"E146"),sQuery(id+"F0.wireOp",EDGE,"E147"),sQuery(id+"F0.wireOp",EDGE,"E148"),sQuery(id+"F0.wireOp",EDGE,"E151"),sQuery(id+"F0.wireOp",EDGE,"E152"),sQuery(id+"F0.wireOp",EDGE,"E153"),sQuery(id+"F0.wireOp",EDGE,"E154"),sQuery(id+"F0.wireOp",EDGE,"E155"),sQuery(id+"F0.wireOp",EDGE,"E156"),sQuery(id+"F0.wireOp",EDGE,"E157"),sQuery(id+"F0.wireOp",EDGE,"E158"),sQuery(id+"F0.wireOp",EDGE,"E159"),sQuery(id+"F0.wireOp",EDGE,"E160"),sQuery(id+"F0.wireOp",EDGE,"E161"),sQuery(id+"F0.wireOp",EDGE,"E162"),sQuery(id+"F0.wireOp",EDGE,"E163"),sQuery(id+"F0.wireOp",EDGE,"E164"),sQuery(id+"F0.wireOp",EDGE,"E165"),sQuery(id+"F0.wireOp",EDGE,"E166"),sQuery(id+"F0.wireOp",EDGE,"E167"),sQuery(id+"F0.wireOp",EDGE,"E168"),sQuery(id+"F7.wireOp",EDGE,"E178"),sQuery(id+"F7.wireOp",EDGE,"E180"),sQuery(id+"F7.wireOp",EDGE,"E181"),subQ2,subQ1,subQ0,sQuery(id+"F30.wireOp",EDGE,"E278.right")])],"isStart":true}),makeQuery(id+"F40.opExtrude","SWEPT_FACE",FACE,{"disambiguationData":[OSD([subQ0]),TDD([makeQuery(id+"F31.opExtrude","CAP_EDGE",EDGE,{"disambiguationData":[OSD([subQ0])],"isStart":true})])]})]}),makeQuery(id+"F41.opExtrude","SWEPT_FACE",FACE,{"disambiguationData":[OSD([subQ2,subQ0]),TDD([makeQuery(id+"F40.boolean.opBoolean","MERGE",EDGE,{"derivedFrom":[makeQuery(id+"F31.opExtrude","CAP_EDGE",EDGE,{"disambiguationData":[OSD([subQ2])],"isStart":true}),makeQuery(id+"F40.opExtrude","SWEPT_EDGE",EDGE,{"disambiguationData":[OSD([subQ2,subQ0]),TDD([makeQuery(id+"F31.opExtrude","CAP_VERTEX",VERTEX,{"disambiguationData":[OSD([subQ2,subQ0])],"isStart":true})])]})]})])]})]}),makeQuery(id+"F42.opExtrude","SWEPT_FACE",FACE,{"disambiguationData":[OSD([subQ1,subQ0]),TDD([makeQuery(id+"F40.boolean.opBoolean","MERGE",EDGE,{"derivedFrom":[makeQuery(id+"F31.opExtrude","CAP_EDGE",EDGE,{"disambiguationData":[OSD([subQ1])],"isStart":true}),makeQuery(id+"F40.opExtrude","SWEPT_EDGE",EDGE,{"disambiguationData":[OSD([subQ1,subQ0]),TDD([makeQuery(id+"F31.opExtrude","CAP_VERTEX",VERTEX,{"disambiguationData":[OSD([subQ1,subQ0])],"isStart":true})])]})]})])]})]}),makeQuery(id+"F65.opExtrude","SWEPT_FACE",FACE,{"disambiguationData":[OSD([sQuery(id+"F64.wireOp",EDGE,"E384")])]})]});}
            var sketch = newSketch(context, id + "F70", { "sketchPlane" : qUnion([Q0])});
            skLineSegment(sketch, "E393", {"start": v(-277.93, -851.15) * mm, "end": v(-277.93, -698.75) * mm});
            skLineSegment(sketch, "E394", {"start": v(-277.93, -698.75) * mm, "end": v(-430.33, -698.75) * mm});
            skLineSegment(sketch, "E395", {"start": v(-430.33, -698.75) * mm, "end": v(-430.33, -851.15) * mm});
            skLineSegment(sketch, "E396", {"start": v(-430.33, -851.15) * mm, "end": v(-277.93, -851.15) * mm});
            skLineSegment(sketch, "E397", {"start": v(230.07, -851.15) * mm, "end": v(230.07, -698.75) * mm});
            skLineSegment(sketch, "E398", {"start": v(230.07, -698.75) * mm, "end": v(382.47, -698.75) * mm});
            skLineSegment(sketch, "E399", {"start": v(382.47, -698.75) * mm, "end": v(382.47, -851.15) * mm});
            skLineSegment(sketch, "E400", {"start": v(382.47, -851.15) * mm, "end": v(230.07, -851.15) * mm});
            skSolve(sketch);
        }
        {
            var Q0;
            Q0 = qSketchRegion(id + "F70", true);
            extrude(context, id + "F71", {"entities" : qUnion([Q0]), "depth" : 177.8 * mm, "offsetDistance" : 25.4 * mm});
        }
        {
            var Q0;
            {var subQ0=sQuery(id+"F63.wireOp",EDGE,"E379");Q0=makeQuery(id+"F63.imprint","IMPRINT",FACE,{"disambiguationData":[TD([[makeQuery(id+"F63.imprint","IMPRINT",EDGE,{"derivedFrom":subQ0}),1.0]])]});}
            extrude(context, id + "F72", {"entities" : qUnion([Q0]), "depth" : 1143 * mm, "offsetDistance" : 25.4 * mm});
        }
        {
            var Q0;
            Q0=makeQuery(id+"F71.opExtrude","SWEPT_FACE",FACE,{"disambiguationData":[OSD([sQuery(id+"F70.wireOp",EDGE,"E399")])]});
            var sketch = newSketch(context, id + "F73", { "sketchPlane" : qUnion([Q0])});
            skLineSegment(sketch, "E401", {"start": v(-774.95, 0) * mm, "end": v(-800.35, 0) * mm});
            skLineSegment(sketch, "E402", {"start": v(-800.35, 0) * mm, "end": v(-749.55, 0) * mm});
            skLineSegment(sketch, "E403", {"start": v(-749.55, 0) * mm, "end": v(-749.55, 101.6) * mm});
            skLineSegment(sketch, "E404", {"start": v(-749.55, 101.6) * mm, "end": v(-800.35, 101.6) * mm});
            skLineSegment(sketch, "E405", {"start": v(-800.35, 101.6) * mm, "end": v(-800.35, 0) * mm});
            skSolve(sketch);
        }
        {
            var Q0;
            Q0 = qSketchRegion(id + "F73", true);
            extrude(context, id + "F74", {"entities" : qUnion([Q0]), "depth" : 635 * mm, "offsetDistance" : 25.4 * mm});
        }
    });
